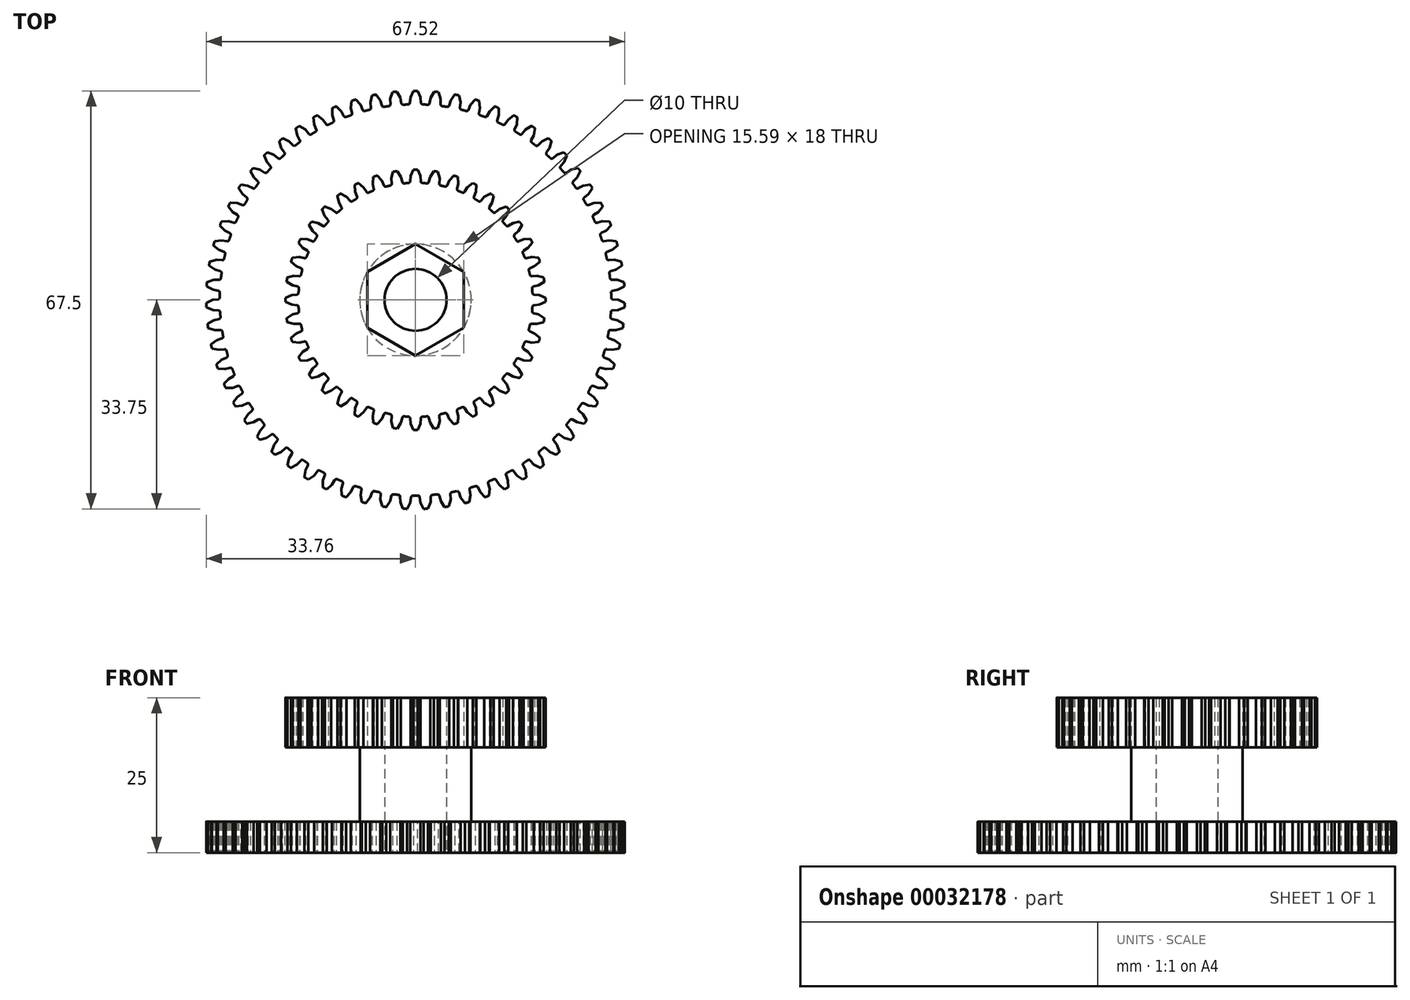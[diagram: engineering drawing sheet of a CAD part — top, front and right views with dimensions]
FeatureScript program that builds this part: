
annotation { "Feature Type Name" : "Feature", "Feature Type Description" : "" }
export const myFeature = defineFeature(function(context is Context, id is Id, definition is map)
    precondition{}
    {
        {
            var Q0;
            Q0=qCreatedBy(makeId("Top.planeOp"),FACE);
            var sketch = newSketch(context, id + "F0", { "sketchPlane" : qUnion([Q0])});
            skArc(sketch, "E0", {"start": v(31.82, 1.48) * mm, "mid": v(31.63, 1.37) * mm, "end": v(31.56, 1.16) * mm});
            skLineSegment(sketch, "E1", {"start": v(31.82, 1.48) * mm, "end": v(32.69, 1.63) * mm});
            skLineSegment(sketch, "E2", {"start": v(32.69, 1.63) * mm, "end": v(33.7, 2.16) * mm});
            skArc(sketch, "E3", {"start": v(31.39, 3.53) * mm, "mid": v(31.34, 3.91) * mm, "end": v(31.29, 4.3) * mm});
            skArc(sketch, "E4", {"start": v(31.81, -1.7) * mm, "mid": v(31.61, -1.79) * mm, "end": v(31.52, -1.99) * mm});
            skArc(sketch, "E5", {"start": v(31.52, 4.64) * mm, "mid": v(31.34, 4.51) * mm, "end": v(31.29, 4.3) * mm});
            skLineSegment(sketch, "E6", {"start": v(31.81, -1.7) * mm, "end": v(32.69, -1.63) * mm});
            skLineSegment(sketch, "E7", {"start": v(31.52, 4.64) * mm, "end": v(32.36, 4.88) * mm});
            skLineSegment(sketch, "E8", {"start": v(32.69, -1.63) * mm, "end": v(33.75, -1.2) * mm});
            skLineSegment(sketch, "E9", {"start": v(32.36, 4.88) * mm, "end": v(33.31, 5.5) * mm});
            skArc(sketch, "E10", {"start": v(30.88, 6.64) * mm, "mid": v(30.8, 7.02) * mm, "end": v(30.7, 7.4) * mm});
            skArc(sketch, "E11", {"start": v(31.49, -4.85) * mm, "mid": v(31.28, -4.93) * mm, "end": v(31.17, -5.12) * mm});
            skArc(sketch, "E12", {"start": v(30.9, 7.76) * mm, "mid": v(30.73, 7.61) * mm, "end": v(30.7, 7.4) * mm});
            skLineSegment(sketch, "E13", {"start": v(31.49, -4.85) * mm, "end": v(32.36, -4.88) * mm});
            skLineSegment(sketch, "E14", {"start": v(30.9, 7.76) * mm, "end": v(31.71, 8.07) * mm});
            skLineSegment(sketch, "E15", {"start": v(32.36, -4.88) * mm, "end": v(33.46, -4.56) * mm});
            skLineSegment(sketch, "E16", {"start": v(31.71, 8.07) * mm, "end": v(32.6, 8.8) * mm});
            skArc(sketch, "E17", {"start": v(30.06, 9.68) * mm, "mid": v(29.94, 10.05) * mm, "end": v(29.81, 10.41) * mm});
            skArc(sketch, "E18", {"start": v(30.85, -7.97) * mm, "mid": v(30.64, -8.02) * mm, "end": v(30.5, -8.2) * mm});
            skArc(sketch, "E19", {"start": v(29.97, 10.8) * mm, "mid": v(29.82, 10.63) * mm, "end": v(29.81, 10.41) * mm});
            skLineSegment(sketch, "E20", {"start": v(30.85, -7.97) * mm, "end": v(31.72, -8.08) * mm});
            skLineSegment(sketch, "E21", {"start": v(29.97, 10.8) * mm, "end": v(30.75, 11.2) * mm});
            skLineSegment(sketch, "E22", {"start": v(31.72, -8.08) * mm, "end": v(32.84, -7.86) * mm});
            skLineSegment(sketch, "E23", {"start": v(30.75, 11.2) * mm, "end": v(31.56, 12) * mm});
            skArc(sketch, "E24", {"start": v(28.95, 12.62) * mm, "mid": v(28.8, 12.98) * mm, "end": v(28.63, 13.33) * mm});
            skArc(sketch, "E25", {"start": v(29.9, -11) * mm, "mid": v(29.69, -11.03) * mm, "end": v(29.54, -11.2) * mm});
            skArc(sketch, "E26", {"start": v(28.74, 13.72) * mm, "mid": v(28.61, 13.55) * mm, "end": v(28.63, 13.33) * mm});
            skLineSegment(sketch, "E27", {"start": v(29.9, -11) * mm, "end": v(30.76, -11.2) * mm});
            skLineSegment(sketch, "E28", {"start": v(28.74, 13.72) * mm, "end": v(29.48, 14.2) * mm});
            skLineSegment(sketch, "E29", {"start": v(30.76, -11.2) * mm, "end": v(31.9, -11.1) * mm});
            skLineSegment(sketch, "E30", {"start": v(29.48, 14.2) * mm, "end": v(30.2, 15.08) * mm});
            skArc(sketch, "E31", {"start": v(27.55, 15.44) * mm, "mid": v(27.35, 15.78) * mm, "end": v(27.16, 16.11) * mm});
            skArc(sketch, "E32", {"start": v(28.66, -13.92) * mm, "mid": v(28.44, -13.93) * mm, "end": v(28.28, -14.08) * mm});
            skArc(sketch, "E33", {"start": v(27.23, 16.52) * mm, "mid": v(27.12, 16.33) * mm, "end": v(27.16, 16.11) * mm});
            skLineSegment(sketch, "E34", {"start": v(28.66, -13.92) * mm, "end": v(29.5, -14.2) * mm});
            skLineSegment(sketch, "E35", {"start": v(27.23, 16.52) * mm, "end": v(27.92, 17.06) * mm});
            skLineSegment(sketch, "E36", {"start": v(29.5, -14.2) * mm, "end": v(30.64, -14.22) * mm});
            skLineSegment(sketch, "E37", {"start": v(27.92, 17.06) * mm, "end": v(28.55, 18.02) * mm});
            skArc(sketch, "E38", {"start": v(25.87, 18.1) * mm, "mid": v(25.65, 18.42) * mm, "end": v(25.42, 18.74) * mm});
            skArc(sketch, "E39", {"start": v(27.13, -16.7) * mm, "mid": v(26.92, -16.69) * mm, "end": v(26.74, -16.82) * mm});
            skArc(sketch, "E40", {"start": v(25.45, 19.15) * mm, "mid": v(25.36, 18.95) * mm, "end": v(25.42, 18.74) * mm});
            skLineSegment(sketch, "E41", {"start": v(27.13, -16.7) * mm, "end": v(27.93, -17.07) * mm});
            skLineSegment(sketch, "E42", {"start": v(25.45, 19.15) * mm, "end": v(26.08, 19.76) * mm});
            skLineSegment(sketch, "E43", {"start": v(27.93, -17.07) * mm, "end": v(29.07, -17.2) * mm});
            skLineSegment(sketch, "E44", {"start": v(26.08, 19.76) * mm, "end": v(26.62, 20.77) * mm});
            skArc(sketch, "E45", {"start": v(23.94, 20.6) * mm, "mid": v(23.68, 20.89) * mm, "end": v(23.42, 21.18) * mm});
            skArc(sketch, "E46", {"start": v(25.34, -19.32) * mm, "mid": v(25.12, -19.29) * mm, "end": v(24.93, -19.4) * mm});
            skArc(sketch, "E47", {"start": v(23.42, 21.59) * mm, "mid": v(23.34, 21.38) * mm, "end": v(23.42, 21.18) * mm});
            skLineSegment(sketch, "E48", {"start": v(25.34, -19.32) * mm, "end": v(26.1, -19.77) * mm});
            skLineSegment(sketch, "E49", {"start": v(23.42, 21.59) * mm, "end": v(23.98, 22.26) * mm});
            skLineSegment(sketch, "E50", {"start": v(26.1, -19.77) * mm, "end": v(27.21, -20) * mm});
            skLineSegment(sketch, "E51", {"start": v(23.98, 22.26) * mm, "end": v(24.41, 23.32) * mm});
            skArc(sketch, "E52", {"start": v(21.77, 22.88) * mm, "mid": v(21.48, 23.14) * mm, "end": v(21.2, 23.4) * mm});
            skArc(sketch, "E53", {"start": v(23.29, -21.75) * mm, "mid": v(23.08, -21.7) * mm, "end": v(22.88, -21.79) * mm});
            skArc(sketch, "E54", {"start": v(21.15, 23.81) * mm, "mid": v(21.1, 23.6) * mm, "end": v(21.2, 23.4) * mm});
            skLineSegment(sketch, "E55", {"start": v(23.29, -21.75) * mm, "end": v(24, -22.27) * mm});
            skLineSegment(sketch, "E56", {"start": v(21.15, 23.81) * mm, "end": v(21.65, 24.53) * mm});
            skLineSegment(sketch, "E57", {"start": v(24, -22.27) * mm, "end": v(25.09, -22.62) * mm});
            skLineSegment(sketch, "E58", {"start": v(21.65, 24.53) * mm, "end": v(21.97, 25.63) * mm});
            skArc(sketch, "E59", {"start": v(19.38, 24.93) * mm, "mid": v(19.07, 25.16) * mm, "end": v(18.76, 25.4) * mm});
            skArc(sketch, "E60", {"start": v(21, -23.96) * mm, "mid": v(20.8, -23.88) * mm, "end": v(20.6, -23.96) * mm});
            skArc(sketch, "E61", {"start": v(18.67, 25.8) * mm, "mid": v(18.64, 25.58) * mm, "end": v(18.76, 25.4) * mm});
            skLineSegment(sketch, "E62", {"start": v(21, -23.96) * mm, "end": v(21.66, -24.55) * mm});
            skLineSegment(sketch, "E63", {"start": v(18.67, 25.8) * mm, "end": v(19.1, 26.57) * mm});
            skLineSegment(sketch, "E64", {"start": v(21.66, -24.55) * mm, "end": v(22.71, -25) * mm});
            skLineSegment(sketch, "E65", {"start": v(19.1, 26.57) * mm, "end": v(19.3, 27.7) * mm});
            skArc(sketch, "E66", {"start": v(16.8, 26.73) * mm, "mid": v(16.47, 26.94) * mm, "end": v(16.14, 27.14) * mm});
            skArc(sketch, "E67", {"start": v(18.52, -25.93) * mm, "mid": v(18.32, -25.84) * mm, "end": v(18.11, -25.89) * mm});
            skArc(sketch, "E68", {"start": v(16.01, 27.53) * mm, "mid": v(16, 27.3) * mm, "end": v(16.14, 27.14) * mm});
            skLineSegment(sketch, "E69", {"start": v(18.52, -25.93) * mm, "end": v(19.11, -26.58) * mm});
            skLineSegment(sketch, "E70", {"start": v(16.01, 27.53) * mm, "end": v(16.35, 28.34) * mm});
            skLineSegment(sketch, "E71", {"start": v(19.11, -26.58) * mm, "end": v(20.11, -27.14) * mm});
            skLineSegment(sketch, "E72", {"start": v(16.35, 28.34) * mm, "end": v(16.45, 29.47) * mm});
            skArc(sketch, "E73", {"start": v(14.05, 28.27) * mm, "mid": v(13.7, 28.44) * mm, "end": v(13.35, 28.61) * mm});
            skArc(sketch, "E74", {"start": v(15.85, -27.65) * mm, "mid": v(15.66, -27.53) * mm, "end": v(15.45, -27.56) * mm});
            skArc(sketch, "E75", {"start": v(13.19, 28.99) * mm, "mid": v(13.2, 28.77) * mm, "end": v(13.35, 28.61) * mm});
            skLineSegment(sketch, "E76", {"start": v(15.85, -27.65) * mm, "end": v(16.37, -28.35) * mm});
            skLineSegment(sketch, "E77", {"start": v(13.19, 28.99) * mm, "end": v(13.45, 29.82) * mm});
            skLineSegment(sketch, "E78", {"start": v(16.37, -28.35) * mm, "end": v(17.31, -29) * mm});
            skLineSegment(sketch, "E79", {"start": v(13.45, 29.82) * mm, "end": v(13.44, 30.97) * mm});
            skArc(sketch, "E80", {"start": v(11.17, 29.53) * mm, "mid": v(10.8, 29.67) * mm, "end": v(10.44, 29.8) * mm});
            skArc(sketch, "E81", {"start": v(13.02, -29.1) * mm, "mid": v(12.84, -28.95) * mm, "end": v(12.63, -28.97) * mm});
            skArc(sketch, "E82", {"start": v(10.24, 30.16) * mm, "mid": v(10.27, 29.94) * mm, "end": v(10.44, 29.8) * mm});
            skLineSegment(sketch, "E83", {"start": v(13.02, -29.1) * mm, "end": v(13.47, -29.84) * mm});
            skLineSegment(sketch, "E84", {"start": v(10.24, 30.16) * mm, "end": v(10.41, 31.01) * mm});
            skLineSegment(sketch, "E85", {"start": v(13.47, -29.84) * mm, "end": v(14.34, -30.59) * mm});
            skLineSegment(sketch, "E86", {"start": v(10.41, 31.01) * mm, "end": v(10.28, 32.15) * mm});
            skArc(sketch, "E87", {"start": v(8.17, 30.5) * mm, "mid": v(7.8, 30.6) * mm, "end": v(7.42, 30.69) * mm});
            skArc(sketch, "E88", {"start": v(10.06, -30.24) * mm, "mid": v(9.9, -30.09) * mm, "end": v(9.68, -30.08) * mm});
            skArc(sketch, "E89", {"start": v(7.18, 31.02) * mm, "mid": v(7.24, 30.81) * mm, "end": v(7.42, 30.69) * mm});
            skLineSegment(sketch, "E90", {"start": v(10.06, -30.24) * mm, "end": v(10.43, -31.03) * mm});
            skLineSegment(sketch, "E91", {"start": v(7.18, 31.02) * mm, "end": v(7.27, 31.9) * mm});
            skLineSegment(sketch, "E92", {"start": v(10.43, -31.03) * mm, "end": v(11.22, -31.86) * mm});
            skLineSegment(sketch, "E93", {"start": v(7.27, 31.9) * mm, "end": v(7.03, 33.01) * mm});
            skArc(sketch, "E94", {"start": v(5.1, 31.16) * mm, "mid": v(4.7, 31.22) * mm, "end": v(4.32, 31.27) * mm});
            skArc(sketch, "E95", {"start": v(7, -31.1) * mm, "mid": v(6.86, -30.93) * mm, "end": v(6.64, -30.9) * mm});
            skArc(sketch, "E96", {"start": v(4.05, 31.59) * mm, "mid": v(4.13, 31.38) * mm, "end": v(4.32, 31.27) * mm});
            skLineSegment(sketch, "E97", {"start": v(7, -31.1) * mm, "end": v(7.3, -31.92) * mm});
            skLineSegment(sketch, "E98", {"start": v(4.05, 31.59) * mm, "end": v(4.06, 32.46) * mm});
            skLineSegment(sketch, "E99", {"start": v(7.3, -31.92) * mm, "end": v(8, -32.82) * mm});
            skLineSegment(sketch, "E100", {"start": v(4.06, 32.46) * mm, "end": v(3.7, 33.55) * mm});
            skArc(sketch, "E101", {"start": v(1.96, 31.51) * mm, "mid": v(1.57, 31.53) * mm, "end": v(1.19, 31.55) * mm});
            skArc(sketch, "E102", {"start": v(3.87, -31.64) * mm, "mid": v(3.74, -31.45) * mm, "end": v(3.53, -31.4) * mm});
            skArc(sketch, "E103", {"start": v(0.89, 31.83) * mm, "mid": v(0.98, 31.63) * mm, "end": v(1.19, 31.55) * mm});
            skLineSegment(sketch, "E104", {"start": v(3.87, -31.64) * mm, "end": v(4.08, -32.49) * mm});
            skLineSegment(sketch, "E105", {"start": v(0.89, 31.83) * mm, "end": v(0.8, 32.7) * mm});
            skLineSegment(sketch, "E106", {"start": v(4.08, -32.49) * mm, "end": v(4.69, -33.45) * mm});
            skLineSegment(sketch, "E107", {"start": v(0.8, 32.7) * mm, "end": v(0.35, 33.75) * mm});
            skArc(sketch, "E108", {"start": v(-1.19, 31.55) * mm, "mid": v(-1.57, 31.53) * mm, "end": v(-1.96, 31.51) * mm});
            skArc(sketch, "E109", {"start": v(0.7, -31.86) * mm, "mid": v(0.6, -31.67) * mm, "end": v(0.39, -31.6) * mm});
            skArc(sketch, "E110", {"start": v(-2.29, 31.76) * mm, "mid": v(-2.17, 31.58) * mm, "end": v(-1.96, 31.51) * mm});
            skLineSegment(sketch, "E111", {"start": v(0.7, -31.86) * mm, "end": v(0.83, -32.73) * mm});
            skLineSegment(sketch, "E112", {"start": v(-2.29, 31.76) * mm, "end": v(-2.46, 32.62) * mm});
            skLineSegment(sketch, "E113", {"start": v(0.83, -32.73) * mm, "end": v(1.34, -33.75) * mm});
            skLineSegment(sketch, "E114", {"start": v(-2.46, 32.62) * mm, "end": v(-3.02, 33.62) * mm});
            skArc(sketch, "E115", {"start": v(-4.32, 31.27) * mm, "mid": v(-4.7, 31.22) * mm, "end": v(-5.1, 31.16) * mm});
            skArc(sketch, "E116", {"start": v(-2.47, -31.77) * mm, "mid": v(-2.56, -31.57) * mm, "end": v(-2.76, -31.48) * mm});
            skArc(sketch, "E117", {"start": v(-5.44, 31.38) * mm, "mid": v(-5.3, 31.2) * mm, "end": v(-5.1, 31.16) * mm});
            skLineSegment(sketch, "E118", {"start": v(-2.47, -31.77) * mm, "end": v(-2.44, -32.65) * mm});
            skLineSegment(sketch, "E119", {"start": v(-5.44, 31.38) * mm, "end": v(-5.7, 32.22) * mm});
            skLineSegment(sketch, "E120", {"start": v(-2.44, -32.65) * mm, "end": v(-2.03, -33.72) * mm});
            skLineSegment(sketch, "E121", {"start": v(-5.7, 32.22) * mm, "end": v(-6.35, 33.15) * mm});
            skArc(sketch, "E122", {"start": v(-7.42, 30.69) * mm, "mid": v(-7.8, 30.6) * mm, "end": v(-8.17, 30.5) * mm});
            skArc(sketch, "E123", {"start": v(-5.62, -31.37) * mm, "mid": v(-5.7, -31.16) * mm, "end": v(-5.88, -31.05) * mm});
            skArc(sketch, "E124", {"start": v(-8.54, 30.68) * mm, "mid": v(-8.39, 30.52) * mm, "end": v(-8.17, 30.5) * mm});
            skLineSegment(sketch, "E125", {"start": v(-5.62, -31.37) * mm, "end": v(-5.67, -32.25) * mm});
            skLineSegment(sketch, "E126", {"start": v(-8.54, 30.68) * mm, "end": v(-8.87, 31.49) * mm});
            skLineSegment(sketch, "E127", {"start": v(-5.67, -32.25) * mm, "end": v(-5.38, -33.35) * mm});
            skLineSegment(sketch, "E128", {"start": v(-8.87, 31.49) * mm, "end": v(-9.62, 32.35) * mm});
            skArc(sketch, "E129", {"start": v(-10.44, 29.8) * mm, "mid": v(-10.8, 29.67) * mm, "end": v(-11.17, 29.53) * mm});
            skArc(sketch, "E130", {"start": v(-8.72, -30.65) * mm, "mid": v(-8.76, -30.44) * mm, "end": v(-8.94, -30.3) * mm});
            skArc(sketch, "E131", {"start": v(-11.55, 29.68) * mm, "mid": v(-11.39, 29.53) * mm, "end": v(-11.17, 29.53) * mm});
            skLineSegment(sketch, "E132", {"start": v(-8.72, -30.65) * mm, "end": v(-8.85, -31.52) * mm});
            skLineSegment(sketch, "E133", {"start": v(-11.55, 29.68) * mm, "end": v(-11.97, 30.45) * mm});
            skLineSegment(sketch, "E134", {"start": v(-8.85, -31.52) * mm, "end": v(-8.67, -32.65) * mm});
            skLineSegment(sketch, "E135", {"start": v(-11.97, 30.45) * mm, "end": v(-12.8, 31.24) * mm});
            skArc(sketch, "E136", {"start": v(-13.35, 28.61) * mm, "mid": v(-13.7, 28.44) * mm, "end": v(-14.05, 28.27) * mm});
            skArc(sketch, "E137", {"start": v(-11.73, -29.63) * mm, "mid": v(-11.75, -29.42) * mm, "end": v(-11.91, -29.27) * mm});
            skArc(sketch, "E138", {"start": v(-14.45, 28.38) * mm, "mid": v(-14.27, 28.25) * mm, "end": v(-14.05, 28.27) * mm});
            skLineSegment(sketch, "E139", {"start": v(-11.73, -29.63) * mm, "end": v(-11.95, -30.48) * mm});
            skLineSegment(sketch, "E140", {"start": v(-14.45, 28.38) * mm, "end": v(-14.94, 29.1) * mm});
            skLineSegment(sketch, "E141", {"start": v(-11.95, -30.48) * mm, "end": v(-11.87, -31.62) * mm});
            skLineSegment(sketch, "E142", {"start": v(-14.94, 29.1) * mm, "end": v(-15.84, 29.8) * mm});
            skArc(sketch, "E143", {"start": v(-16.14, 27.14) * mm, "mid": v(-16.47, 26.94) * mm, "end": v(-16.8, 26.73) * mm});
            skArc(sketch, "E144", {"start": v(-14.62, -28.32) * mm, "mid": v(-14.62, -28.1) * mm, "end": v(-14.76, -27.94) * mm});
            skArc(sketch, "E145", {"start": v(-17.2, 26.8) * mm, "mid": v(-17.01, 26.7) * mm, "end": v(-16.8, 26.73) * mm});
            skLineSegment(sketch, "E146", {"start": v(-14.62, -28.32) * mm, "end": v(-14.92, -29.14) * mm});
            skLineSegment(sketch, "E147", {"start": v(-17.2, 26.8) * mm, "end": v(-17.77, 27.47) * mm});
            skLineSegment(sketch, "E148", {"start": v(-14.92, -29.14) * mm, "end": v(-14.96, -30.28) * mm});
            skLineSegment(sketch, "E149", {"start": v(-17.77, 27.47) * mm, "end": v(-18.73, 28.08) * mm});
            skArc(sketch, "E150", {"start": v(-18.76, 25.4) * mm, "mid": v(-19.07, 25.16) * mm, "end": v(-19.38, 24.93) * mm});
            skArc(sketch, "E151", {"start": v(-17.36, -26.72) * mm, "mid": v(-17.34, -26.5) * mm, "end": v(-17.47, -26.33) * mm});
            skArc(sketch, "E152", {"start": v(-19.79, 24.95) * mm, "mid": v(-19.59, 24.86) * mm, "end": v(-19.38, 24.93) * mm});
            skLineSegment(sketch, "E153", {"start": v(-17.36, -26.72) * mm, "end": v(-17.75, -27.51) * mm});
            skLineSegment(sketch, "E154", {"start": v(-19.79, 24.95) * mm, "end": v(-20.41, 25.57) * mm});
            skLineSegment(sketch, "E155", {"start": v(-17.75, -27.51) * mm, "end": v(-17.9, -28.64) * mm});
            skLineSegment(sketch, "E156", {"start": v(-20.41, 25.57) * mm, "end": v(-21.44, 26.08) * mm});
            skArc(sketch, "E157", {"start": v(-21.2, 23.4) * mm, "mid": v(-21.48, 23.14) * mm, "end": v(-21.77, 22.88) * mm});
            skArc(sketch, "E158", {"start": v(-19.94, -24.86) * mm, "mid": v(-19.9, -24.65) * mm, "end": v(-20, -24.46) * mm});
            skArc(sketch, "E159", {"start": v(-22.18, 22.86) * mm, "mid": v(-21.97, 22.79) * mm, "end": v(-21.77, 22.88) * mm});
            skLineSegment(sketch, "E160", {"start": v(-19.94, -24.86) * mm, "end": v(-20.4, -25.6) * mm});
            skLineSegment(sketch, "E161", {"start": v(-22.18, 22.86) * mm, "end": v(-22.86, 23.4) * mm});
            skLineSegment(sketch, "E162", {"start": v(-20.4, -25.6) * mm, "end": v(-20.66, -26.72) * mm});
            skLineSegment(sketch, "E163", {"start": v(-22.86, 23.4) * mm, "end": v(-23.93, 23.81) * mm});
            skArc(sketch, "E164", {"start": v(-23.42, 21.18) * mm, "mid": v(-23.68, 20.89) * mm, "end": v(-23.94, 20.6) * mm});
            skArc(sketch, "E165", {"start": v(-22.31, -22.75) * mm, "mid": v(-22.25, -22.54) * mm, "end": v(-22.34, -22.34) * mm});
            skArc(sketch, "E166", {"start": v(-24.34, 20.54) * mm, "mid": v(-24.13, 20.49) * mm, "end": v(-23.94, 20.6) * mm});
            skLineSegment(sketch, "E167", {"start": v(-22.31, -22.75) * mm, "end": v(-22.84, -23.45) * mm});
            skLineSegment(sketch, "E168", {"start": v(-24.34, 20.54) * mm, "end": v(-25.08, 21.02) * mm});
            skLineSegment(sketch, "E169", {"start": v(-22.84, -23.45) * mm, "end": v(-23.22, -24.53) * mm});
            skLineSegment(sketch, "E170", {"start": v(-25.08, 21.02) * mm, "end": v(-26.18, 21.31) * mm});
            skArc(sketch, "E171", {"start": v(-25.42, 18.74) * mm, "mid": v(-25.65, 18.42) * mm, "end": v(-25.87, 18.1) * mm});
            skArc(sketch, "E172", {"start": v(-24.46, -20.42) * mm, "mid": v(-24.38, -20.22) * mm, "end": v(-24.45, -20) * mm});
            skArc(sketch, "E173", {"start": v(-26.27, 18.01) * mm, "mid": v(-26.05, 17.98) * mm, "end": v(-25.87, 18.1) * mm});
            skLineSegment(sketch, "E174", {"start": v(-24.46, -20.42) * mm, "end": v(-25.06, -21.06) * mm});
            skLineSegment(sketch, "E175", {"start": v(-26.27, 18.01) * mm, "end": v(-27.05, 18.41) * mm});
            skLineSegment(sketch, "E176", {"start": v(-25.06, -21.06) * mm, "end": v(-25.55, -22.1) * mm});
            skLineSegment(sketch, "E177", {"start": v(-27.05, 18.41) * mm, "end": v(-28.18, 18.6) * mm});
            skArc(sketch, "E178", {"start": v(-27.16, 16.11) * mm, "mid": v(-27.35, 15.78) * mm, "end": v(-27.55, 15.44) * mm});
            skArc(sketch, "E179", {"start": v(-26.37, -17.88) * mm, "mid": v(-26.27, -17.69) * mm, "end": v(-26.32, -17.47) * mm});
            skArc(sketch, "E180", {"start": v(-27.93, 15.3) * mm, "mid": v(-27.71, 15.3) * mm, "end": v(-27.55, 15.44) * mm});
            skLineSegment(sketch, "E181", {"start": v(-26.37, -17.88) * mm, "end": v(-27.04, -18.46) * mm});
            skLineSegment(sketch, "E182", {"start": v(-27.93, 15.3) * mm, "end": v(-28.75, 15.63) * mm});
            skLineSegment(sketch, "E183", {"start": v(-27.04, -18.46) * mm, "end": v(-27.62, -19.44) * mm});
            skLineSegment(sketch, "E184", {"start": v(-28.75, 15.63) * mm, "end": v(-29.89, 15.7) * mm});
            skArc(sketch, "E185", {"start": v(-28.63, 13.33) * mm, "mid": v(-28.8, 12.98) * mm, "end": v(-28.95, 12.62) * mm});
            skArc(sketch, "E186", {"start": v(-28.02, -15.17) * mm, "mid": v(-27.9, -14.98) * mm, "end": v(-27.93, -14.77) * mm});
            skArc(sketch, "E187", {"start": v(-29.32, 12.45) * mm, "mid": v(-29.1, 12.47) * mm, "end": v(-28.95, 12.62) * mm});
            skLineSegment(sketch, "E188", {"start": v(-28.02, -15.17) * mm, "end": v(-28.74, -15.68) * mm});
            skLineSegment(sketch, "E189", {"start": v(-29.32, 12.45) * mm, "end": v(-30.16, 12.69) * mm});
            skLineSegment(sketch, "E190", {"start": v(-28.74, -15.68) * mm, "end": v(-29.42, -16.6) * mm});
            skLineSegment(sketch, "E191", {"start": v(-30.16, 12.69) * mm, "end": v(-31.3, 12.65) * mm});
            skArc(sketch, "E192", {"start": v(-29.82, 10.41) * mm, "mid": v(-29.94, 10.05) * mm, "end": v(-30.06, 9.68) * mm});
            skArc(sketch, "E193", {"start": v(-29.4, -12.3) * mm, "mid": v(-29.25, -12.13) * mm, "end": v(-29.26, -11.91) * mm});
            skArc(sketch, "E194", {"start": v(-30.41, 9.47) * mm, "mid": v(-30.2, 9.5) * mm, "end": v(-30.06, 9.68) * mm});
            skLineSegment(sketch, "E195", {"start": v(-29.4, -12.3) * mm, "end": v(-30.15, -12.74) * mm});
            skLineSegment(sketch, "E196", {"start": v(-30.41, 9.47) * mm, "end": v(-31.28, 9.62) * mm});
            skLineSegment(sketch, "E197", {"start": v(-30.15, -12.74) * mm, "end": v(-30.92, -13.58) * mm});
            skLineSegment(sketch, "E198", {"start": v(-31.28, 9.62) * mm, "end": v(-32.4, 9.47) * mm});
            skArc(sketch, "E199", {"start": v(-30.7, 7.4) * mm, "mid": v(-30.8, 7.02) * mm, "end": v(-30.88, 6.64) * mm});
            skArc(sketch, "E200", {"start": v(-30.47, -9.31) * mm, "mid": v(-30.31, -9.16) * mm, "end": v(-30.3, -8.94) * mm});
            skArc(sketch, "E201", {"start": v(-31.2, 6.4) * mm, "mid": v(-31, 6.45) * mm, "end": v(-30.88, 6.64) * mm});
            skLineSegment(sketch, "E202", {"start": v(-30.47, -9.31) * mm, "end": v(-31.27, -9.67) * mm});
            skLineSegment(sketch, "E203", {"start": v(-31.2, 6.4) * mm, "end": v(-32.08, 6.46) * mm});
            skLineSegment(sketch, "E204", {"start": v(-31.27, -9.67) * mm, "end": v(-32.12, -10.44) * mm});
            skLineSegment(sketch, "E205", {"start": v(-32.08, 6.46) * mm, "end": v(-33.2, 6.2) * mm});
            skArc(sketch, "E206", {"start": v(-31.29, 4.3) * mm, "mid": v(-31.34, 3.91) * mm, "end": v(-31.39, 3.53) * mm});
            skArc(sketch, "E207", {"start": v(-31.24, -6.23) * mm, "mid": v(-31.07, -6.1) * mm, "end": v(-31.04, -5.88) * mm});
            skArc(sketch, "E208", {"start": v(-31.69, 3.25) * mm, "mid": v(-31.49, 3.33) * mm, "end": v(-31.39, 3.53) * mm});
            skLineSegment(sketch, "E209", {"start": v(-31.24, -6.23) * mm, "end": v(-32.08, -6.5) * mm});
            skLineSegment(sketch, "E210", {"start": v(-31.69, 3.25) * mm, "end": v(-32.57, 3.23) * mm});
            skLineSegment(sketch, "E211", {"start": v(-32.08, -6.5) * mm, "end": v(-33, -7.19) * mm});
            skLineSegment(sketch, "E212", {"start": v(-32.57, 3.23) * mm, "end": v(-33.65, 2.86) * mm});
            skArc(sketch, "E213", {"start": v(-31.7, -3.1) * mm, "mid": v(-31.52, -2.97) * mm, "end": v(-31.47, -2.76) * mm});
            skArc(sketch, "E214", {"start": v(-31.56, 1.16) * mm, "mid": v(-31.58, 0.77) * mm, "end": v(-31.58, 0.39) * mm});
            skLineSegment(sketch, "E215", {"start": v(-31.7, -3.1) * mm, "end": v(-32.56, -3.28) * mm});
            skArc(sketch, "E216", {"start": v(-31.86, 0.08) * mm, "mid": v(-31.66, 0.18) * mm, "end": v(-31.58, 0.39) * mm});
            skLineSegment(sketch, "E217", {"start": v(-32.56, -3.28) * mm, "end": v(-33.55, -3.87) * mm});
            skLineSegment(sketch, "E218", {"start": v(-31.86, 0.08) * mm, "end": v(-32.73, -0.02) * mm});
            skLineSegment(sketch, "E219", {"start": v(-32.73, -0.02) * mm, "end": v(-33.76, -0.5) * mm});
            skLineSegment(sketch, "E220", {"start": v(-33.75, -1.2) * mm, "end": v(-32.69, -1.63) * mm});
            skLineSegment(sketch, "E221", {"start": v(-32.69, -1.63) * mm, "end": v(-31.81, -1.7) * mm});
            skArc(sketch, "E222", {"start": v(-31.52, -1.99) * mm, "mid": v(-31.61, -1.79) * mm, "end": v(-31.81, -1.7) * mm});
            skArc(sketch, "E223", {"start": v(-31.52, -1.99) * mm, "mid": v(-31.5, -2.37) * mm, "end": v(-31.47, -2.76) * mm});
            skLineSegment(sketch, "E224", {"start": v(-33.46, -4.56) * mm, "end": v(-32.36, -4.88) * mm});
            skLineSegment(sketch, "E225", {"start": v(-32.36, -4.88) * mm, "end": v(-31.49, -4.85) * mm});
            skArc(sketch, "E226", {"start": v(-31.17, -5.12) * mm, "mid": v(-31.28, -4.93) * mm, "end": v(-31.49, -4.85) * mm});
            skArc(sketch, "E227", {"start": v(-31.17, -5.12) * mm, "mid": v(-31.1, -5.5) * mm, "end": v(-31.04, -5.88) * mm});
            skLineSegment(sketch, "E228", {"start": v(-32.84, -7.86) * mm, "end": v(-31.72, -8.08) * mm});
            skLineSegment(sketch, "E229", {"start": v(-31.72, -8.08) * mm, "end": v(-30.85, -7.97) * mm});
            skArc(sketch, "E230", {"start": v(-30.5, -8.2) * mm, "mid": v(-30.64, -8.02) * mm, "end": v(-30.85, -7.97) * mm});
            skArc(sketch, "E231", {"start": v(-30.5, -8.2) * mm, "mid": v(-30.4, -8.57) * mm, "end": v(-30.3, -8.94) * mm});
            skLineSegment(sketch, "E232", {"start": v(-31.9, -11.1) * mm, "end": v(-30.76, -11.2) * mm});
            skLineSegment(sketch, "E233", {"start": v(-30.76, -11.2) * mm, "end": v(-29.9, -11) * mm});
            skArc(sketch, "E234", {"start": v(-29.54, -11.2) * mm, "mid": v(-29.69, -11.03) * mm, "end": v(-29.9, -11) * mm});
            skArc(sketch, "E235", {"start": v(-29.54, -11.2) * mm, "mid": v(-29.4, -11.55) * mm, "end": v(-29.26, -11.91) * mm});
            skLineSegment(sketch, "E236", {"start": v(-30.64, -14.22) * mm, "end": v(-29.5, -14.2) * mm});
            skLineSegment(sketch, "E237", {"start": v(-29.5, -14.2) * mm, "end": v(-28.66, -13.92) * mm});
            skArc(sketch, "E238", {"start": v(-28.28, -14.08) * mm, "mid": v(-28.44, -13.93) * mm, "end": v(-28.66, -13.92) * mm});
            skArc(sketch, "E239", {"start": v(-28.28, -14.08) * mm, "mid": v(-28.1, -14.42) * mm, "end": v(-27.93, -14.77) * mm});
            skLineSegment(sketch, "E240", {"start": v(-29.07, -17.2) * mm, "end": v(-27.93, -17.07) * mm});
            skLineSegment(sketch, "E241", {"start": v(-27.93, -17.07) * mm, "end": v(-27.13, -16.7) * mm});
            skArc(sketch, "E242", {"start": v(-26.74, -16.82) * mm, "mid": v(-26.92, -16.69) * mm, "end": v(-27.13, -16.7) * mm});
            skArc(sketch, "E243", {"start": v(-26.74, -16.82) * mm, "mid": v(-26.53, -17.15) * mm, "end": v(-26.32, -17.47) * mm});
            skLineSegment(sketch, "E244", {"start": v(-27.21, -20) * mm, "end": v(-26.1, -19.77) * mm});
            skLineSegment(sketch, "E245", {"start": v(-26.1, -19.77) * mm, "end": v(-25.34, -19.32) * mm});
            skArc(sketch, "E246", {"start": v(-24.93, -19.4) * mm, "mid": v(-25.12, -19.29) * mm, "end": v(-25.34, -19.32) * mm});
            skArc(sketch, "E247", {"start": v(-24.93, -19.4) * mm, "mid": v(-24.7, -19.7) * mm, "end": v(-24.45, -20) * mm});
            skLineSegment(sketch, "E248", {"start": v(-25.09, -22.62) * mm, "end": v(-24, -22.27) * mm});
            skLineSegment(sketch, "E249", {"start": v(-24, -22.27) * mm, "end": v(-23.29, -21.75) * mm});
            skArc(sketch, "E250", {"start": v(-22.88, -21.79) * mm, "mid": v(-23.08, -21.7) * mm, "end": v(-23.29, -21.75) * mm});
            skArc(sketch, "E251", {"start": v(-22.88, -21.79) * mm, "mid": v(-22.61, -22.07) * mm, "end": v(-22.34, -22.34) * mm});
            skLineSegment(sketch, "E252", {"start": v(-22.71, -25) * mm, "end": v(-21.66, -24.55) * mm});
            skLineSegment(sketch, "E253", {"start": v(-21.66, -24.55) * mm, "end": v(-21, -23.96) * mm});
            skArc(sketch, "E254", {"start": v(-20.6, -23.96) * mm, "mid": v(-20.8, -23.88) * mm, "end": v(-21, -23.96) * mm});
            skArc(sketch, "E255", {"start": v(-20.6, -23.96) * mm, "mid": v(-20.3, -24.2) * mm, "end": v(-20, -24.46) * mm});
            skLineSegment(sketch, "E256", {"start": v(-20.11, -27.14) * mm, "end": v(-19.11, -26.58) * mm});
            skLineSegment(sketch, "E257", {"start": v(-19.11, -26.58) * mm, "end": v(-18.52, -25.93) * mm});
            skArc(sketch, "E258", {"start": v(-18.11, -25.89) * mm, "mid": v(-18.32, -25.84) * mm, "end": v(-18.52, -25.93) * mm});
            skArc(sketch, "E259", {"start": v(-18.11, -25.89) * mm, "mid": v(-17.8, -26.11) * mm, "end": v(-17.47, -26.33) * mm});
            skLineSegment(sketch, "E260", {"start": v(-17.31, -29) * mm, "end": v(-16.37, -28.35) * mm});
            skLineSegment(sketch, "E261", {"start": v(-16.37, -28.35) * mm, "end": v(-15.85, -27.65) * mm});
            skArc(sketch, "E262", {"start": v(-15.45, -27.56) * mm, "mid": v(-15.66, -27.53) * mm, "end": v(-15.85, -27.65) * mm});
            skArc(sketch, "E263", {"start": v(-15.45, -27.56) * mm, "mid": v(-15.1, -27.75) * mm, "end": v(-14.76, -27.94) * mm});
            skLineSegment(sketch, "E264", {"start": v(-14.34, -30.59) * mm, "end": v(-13.47, -29.84) * mm});
            skLineSegment(sketch, "E265", {"start": v(-13.47, -29.84) * mm, "end": v(-13.02, -29.1) * mm});
            skArc(sketch, "E266", {"start": v(-12.63, -28.97) * mm, "mid": v(-12.84, -28.95) * mm, "end": v(-13.02, -29.1) * mm});
            skArc(sketch, "E267", {"start": v(-12.63, -28.97) * mm, "mid": v(-12.27, -29.12) * mm, "end": v(-11.91, -29.27) * mm});
            skLineSegment(sketch, "E268", {"start": v(-11.22, -31.86) * mm, "end": v(-10.43, -31.03) * mm});
            skLineSegment(sketch, "E269", {"start": v(-10.43, -31.03) * mm, "end": v(-10.06, -30.24) * mm});
            skArc(sketch, "E270", {"start": v(-9.68, -30.08) * mm, "mid": v(-9.9, -30.09) * mm, "end": v(-10.06, -30.24) * mm});
            skArc(sketch, "E271", {"start": v(-9.68, -30.08) * mm, "mid": v(-9.3, -30.2) * mm, "end": v(-8.94, -30.3) * mm});
            skLineSegment(sketch, "E272", {"start": v(-8, -32.82) * mm, "end": v(-7.3, -31.92) * mm});
            skLineSegment(sketch, "E273", {"start": v(-7.3, -31.92) * mm, "end": v(-7, -31.1) * mm});
            skArc(sketch, "E274", {"start": v(-6.64, -30.9) * mm, "mid": v(-6.86, -30.93) * mm, "end": v(-7, -31.1) * mm});
            skArc(sketch, "E275", {"start": v(-6.64, -30.9) * mm, "mid": v(-6.26, -30.97) * mm, "end": v(-5.88, -31.05) * mm});
            skLineSegment(sketch, "E276", {"start": v(-4.69, -33.45) * mm, "end": v(-4.08, -32.49) * mm});
            skLineSegment(sketch, "E277", {"start": v(-4.08, -32.49) * mm, "end": v(-3.87, -31.64) * mm});
            skArc(sketch, "E278", {"start": v(-3.53, -31.4) * mm, "mid": v(-3.74, -31.45) * mm, "end": v(-3.87, -31.64) * mm});
            skArc(sketch, "E279", {"start": v(-3.53, -31.4) * mm, "mid": v(-3.14, -31.44) * mm, "end": v(-2.76, -31.48) * mm});
            skLineSegment(sketch, "E280", {"start": v(-1.34, -33.75) * mm, "end": v(-0.83, -32.73) * mm});
            skLineSegment(sketch, "E281", {"start": v(-0.83, -32.73) * mm, "end": v(-0.7, -31.86) * mm});
            skArc(sketch, "E282", {"start": v(-0.39, -31.6) * mm, "mid": v(-0.6, -31.67) * mm, "end": v(-0.7, -31.86) * mm});
            skArc(sketch, "E283", {"start": v(-0.39, -31.6) * mm, "mid": v(0, -31.6) * mm, "end": v(0.39, -31.6) * mm});
            skLineSegment(sketch, "E284", {"start": v(2.03, -33.72) * mm, "end": v(2.44, -32.65) * mm});
            skLineSegment(sketch, "E285", {"start": v(2.44, -32.65) * mm, "end": v(2.47, -31.77) * mm});
            skArc(sketch, "E286", {"start": v(2.76, -31.48) * mm, "mid": v(2.56, -31.57) * mm, "end": v(2.47, -31.77) * mm});
            skArc(sketch, "E287", {"start": v(2.76, -31.48) * mm, "mid": v(3.14, -31.44) * mm, "end": v(3.53, -31.4) * mm});
            skLineSegment(sketch, "E288", {"start": v(5.38, -33.35) * mm, "end": v(5.67, -32.25) * mm});
            skLineSegment(sketch, "E289", {"start": v(5.67, -32.25) * mm, "end": v(5.62, -31.37) * mm});
            skArc(sketch, "E290", {"start": v(5.88, -31.05) * mm, "mid": v(5.7, -31.16) * mm, "end": v(5.62, -31.37) * mm});
            skArc(sketch, "E291", {"start": v(5.88, -31.05) * mm, "mid": v(6.26, -30.97) * mm, "end": v(6.64, -30.9) * mm});
            skLineSegment(sketch, "E292", {"start": v(8.67, -32.65) * mm, "end": v(8.85, -31.52) * mm});
            skLineSegment(sketch, "E293", {"start": v(8.85, -31.52) * mm, "end": v(8.72, -30.65) * mm});
            skArc(sketch, "E294", {"start": v(8.94, -30.3) * mm, "mid": v(8.76, -30.44) * mm, "end": v(8.72, -30.65) * mm});
            skArc(sketch, "E295", {"start": v(8.94, -30.3) * mm, "mid": v(9.3, -30.2) * mm, "end": v(9.68, -30.08) * mm});
            skLineSegment(sketch, "E296", {"start": v(11.87, -31.62) * mm, "end": v(11.95, -30.48) * mm});
            skLineSegment(sketch, "E297", {"start": v(11.95, -30.48) * mm, "end": v(11.73, -29.63) * mm});
            skArc(sketch, "E298", {"start": v(11.91, -29.27) * mm, "mid": v(11.75, -29.42) * mm, "end": v(11.73, -29.63) * mm});
            skArc(sketch, "E299", {"start": v(11.91, -29.27) * mm, "mid": v(12.27, -29.12) * mm, "end": v(12.63, -28.97) * mm});
            skLineSegment(sketch, "E300", {"start": v(14.96, -30.28) * mm, "end": v(14.92, -29.14) * mm});
            skLineSegment(sketch, "E301", {"start": v(14.92, -29.14) * mm, "end": v(14.62, -28.32) * mm});
            skArc(sketch, "E302", {"start": v(14.76, -27.94) * mm, "mid": v(14.62, -28.1) * mm, "end": v(14.62, -28.32) * mm});
            skArc(sketch, "E303", {"start": v(14.76, -27.94) * mm, "mid": v(15.1, -27.75) * mm, "end": v(15.45, -27.56) * mm});
            skLineSegment(sketch, "E304", {"start": v(17.9, -28.64) * mm, "end": v(17.75, -27.51) * mm});
            skLineSegment(sketch, "E305", {"start": v(17.75, -27.51) * mm, "end": v(17.36, -26.72) * mm});
            skArc(sketch, "E306", {"start": v(17.47, -26.33) * mm, "mid": v(17.34, -26.5) * mm, "end": v(17.36, -26.72) * mm});
            skArc(sketch, "E307", {"start": v(17.47, -26.33) * mm, "mid": v(17.8, -26.11) * mm, "end": v(18.11, -25.89) * mm});
            skLineSegment(sketch, "E308", {"start": v(20.66, -26.72) * mm, "end": v(20.4, -25.6) * mm});
            skLineSegment(sketch, "E309", {"start": v(20.4, -25.6) * mm, "end": v(19.94, -24.86) * mm});
            skArc(sketch, "E310", {"start": v(20, -24.46) * mm, "mid": v(19.9, -24.65) * mm, "end": v(19.94, -24.86) * mm});
            skArc(sketch, "E311", {"start": v(20, -24.46) * mm, "mid": v(20.3, -24.2) * mm, "end": v(20.6, -23.96) * mm});
            skLineSegment(sketch, "E312", {"start": v(23.22, -24.53) * mm, "end": v(22.84, -23.45) * mm});
            skLineSegment(sketch, "E313", {"start": v(22.84, -23.45) * mm, "end": v(22.31, -22.75) * mm});
            skArc(sketch, "E314", {"start": v(22.34, -22.34) * mm, "mid": v(22.25, -22.54) * mm, "end": v(22.31, -22.75) * mm});
            skArc(sketch, "E315", {"start": v(22.34, -22.34) * mm, "mid": v(22.61, -22.07) * mm, "end": v(22.88, -21.79) * mm});
            skLineSegment(sketch, "E316", {"start": v(25.55, -22.1) * mm, "end": v(25.06, -21.06) * mm});
            skLineSegment(sketch, "E317", {"start": v(25.06, -21.06) * mm, "end": v(24.46, -20.42) * mm});
            skArc(sketch, "E318", {"start": v(24.45, -20) * mm, "mid": v(24.38, -20.22) * mm, "end": v(24.46, -20.42) * mm});
            skArc(sketch, "E319", {"start": v(24.45, -20) * mm, "mid": v(24.7, -19.7) * mm, "end": v(24.93, -19.4) * mm});
            skLineSegment(sketch, "E320", {"start": v(27.62, -19.44) * mm, "end": v(27.04, -18.46) * mm});
            skLineSegment(sketch, "E321", {"start": v(27.04, -18.46) * mm, "end": v(26.37, -17.88) * mm});
            skArc(sketch, "E322", {"start": v(26.32, -17.47) * mm, "mid": v(26.27, -17.69) * mm, "end": v(26.37, -17.88) * mm});
            skArc(sketch, "E323", {"start": v(26.32, -17.47) * mm, "mid": v(26.53, -17.15) * mm, "end": v(26.74, -16.82) * mm});
            skLineSegment(sketch, "E324", {"start": v(29.42, -16.6) * mm, "end": v(28.74, -15.68) * mm});
            skLineSegment(sketch, "E325", {"start": v(28.74, -15.68) * mm, "end": v(28.02, -15.17) * mm});
            skArc(sketch, "E326", {"start": v(27.93, -14.77) * mm, "mid": v(27.9, -14.98) * mm, "end": v(28.02, -15.17) * mm});
            skArc(sketch, "E327", {"start": v(27.93, -14.77) * mm, "mid": v(28.1, -14.42) * mm, "end": v(28.28, -14.08) * mm});
            skLineSegment(sketch, "E328", {"start": v(30.92, -13.58) * mm, "end": v(30.15, -12.74) * mm});
            skLineSegment(sketch, "E329", {"start": v(30.15, -12.74) * mm, "end": v(29.4, -12.3) * mm});
            skArc(sketch, "E330", {"start": v(29.26, -11.91) * mm, "mid": v(29.25, -12.13) * mm, "end": v(29.4, -12.3) * mm});
            skArc(sketch, "E331", {"start": v(29.26, -11.91) * mm, "mid": v(29.4, -11.55) * mm, "end": v(29.54, -11.2) * mm});
            skLineSegment(sketch, "E332", {"start": v(32.12, -10.44) * mm, "end": v(31.27, -9.67) * mm});
            skLineSegment(sketch, "E333", {"start": v(31.27, -9.67) * mm, "end": v(30.47, -9.31) * mm});
            skArc(sketch, "E334", {"start": v(30.3, -8.94) * mm, "mid": v(30.31, -9.16) * mm, "end": v(30.47, -9.31) * mm});
            skArc(sketch, "E335", {"start": v(30.3, -8.94) * mm, "mid": v(30.4, -8.57) * mm, "end": v(30.5, -8.2) * mm});
            skLineSegment(sketch, "E336", {"start": v(33, -7.19) * mm, "end": v(32.08, -6.5) * mm});
            skLineSegment(sketch, "E337", {"start": v(32.08, -6.5) * mm, "end": v(31.24, -6.23) * mm});
            skArc(sketch, "E338", {"start": v(31.04, -5.88) * mm, "mid": v(31.07, -6.1) * mm, "end": v(31.24, -6.23) * mm});
            skArc(sketch, "E339", {"start": v(31.04, -5.88) * mm, "mid": v(31.1, -5.5) * mm, "end": v(31.17, -5.12) * mm});
            skLineSegment(sketch, "E340", {"start": v(33.55, -3.87) * mm, "end": v(32.56, -3.28) * mm});
            skLineSegment(sketch, "E341", {"start": v(32.56, -3.28) * mm, "end": v(31.7, -3.1) * mm});
            skArc(sketch, "E342", {"start": v(31.47, -2.76) * mm, "mid": v(31.52, -2.97) * mm, "end": v(31.7, -3.1) * mm});
            skArc(sketch, "E343", {"start": v(31.47, -2.76) * mm, "mid": v(31.5, -2.37) * mm, "end": v(31.52, -1.99) * mm});
            skLineSegment(sketch, "E344", {"start": v(33.76, -0.5) * mm, "end": v(32.73, -0.02) * mm});
            skLineSegment(sketch, "E345", {"start": v(32.73, -0.02) * mm, "end": v(31.86, 0.08) * mm});
            skArc(sketch, "E346", {"start": v(31.58, 0.39) * mm, "mid": v(31.66, 0.18) * mm, "end": v(31.86, 0.08) * mm});
            skArc(sketch, "E347", {"start": v(31.58, 0.39) * mm, "mid": v(31.58, 0.77) * mm, "end": v(31.56, 1.16) * mm});
            skLineSegment(sketch, "E348", {"start": v(33.65, 2.86) * mm, "end": v(32.57, 3.23) * mm});
            skLineSegment(sketch, "E349", {"start": v(32.57, 3.23) * mm, "end": v(31.69, 3.25) * mm});
            skArc(sketch, "E350", {"start": v(31.39, 3.53) * mm, "mid": v(31.49, 3.33) * mm, "end": v(31.69, 3.25) * mm});
            skLineSegment(sketch, "E351", {"start": v(33.2, 6.2) * mm, "end": v(32.08, 6.46) * mm});
            skLineSegment(sketch, "E352", {"start": v(32.08, 6.46) * mm, "end": v(31.2, 6.4) * mm});
            skArc(sketch, "E353", {"start": v(30.88, 6.64) * mm, "mid": v(31, 6.45) * mm, "end": v(31.2, 6.4) * mm});
            skLineSegment(sketch, "E354", {"start": v(32.4, 9.47) * mm, "end": v(31.28, 9.62) * mm});
            skLineSegment(sketch, "E355", {"start": v(31.28, 9.62) * mm, "end": v(30.41, 9.47) * mm});
            skArc(sketch, "E356", {"start": v(30.06, 9.68) * mm, "mid": v(30.2, 9.5) * mm, "end": v(30.41, 9.47) * mm});
            skLineSegment(sketch, "E357", {"start": v(31.3, 12.65) * mm, "end": v(30.16, 12.69) * mm});
            skLineSegment(sketch, "E358", {"start": v(30.16, 12.69) * mm, "end": v(29.32, 12.45) * mm});
            skArc(sketch, "E359", {"start": v(28.95, 12.62) * mm, "mid": v(29.1, 12.47) * mm, "end": v(29.32, 12.45) * mm});
            skLineSegment(sketch, "E360", {"start": v(29.89, 15.7) * mm, "end": v(28.75, 15.63) * mm});
            skLineSegment(sketch, "E361", {"start": v(28.75, 15.63) * mm, "end": v(27.93, 15.3) * mm});
            skArc(sketch, "E362", {"start": v(27.55, 15.44) * mm, "mid": v(27.71, 15.3) * mm, "end": v(27.93, 15.3) * mm});
            skLineSegment(sketch, "E363", {"start": v(28.18, 18.6) * mm, "end": v(27.05, 18.41) * mm});
            skLineSegment(sketch, "E364", {"start": v(27.05, 18.41) * mm, "end": v(26.27, 18.01) * mm});
            skArc(sketch, "E365", {"start": v(25.87, 18.1) * mm, "mid": v(26.05, 17.98) * mm, "end": v(26.27, 18.01) * mm});
            skLineSegment(sketch, "E366", {"start": v(26.18, 21.31) * mm, "end": v(25.08, 21.02) * mm});
            skLineSegment(sketch, "E367", {"start": v(25.08, 21.02) * mm, "end": v(24.34, 20.54) * mm});
            skArc(sketch, "E368", {"start": v(23.94, 20.6) * mm, "mid": v(24.13, 20.49) * mm, "end": v(24.34, 20.54) * mm});
            skLineSegment(sketch, "E369", {"start": v(23.93, 23.81) * mm, "end": v(22.86, 23.4) * mm});
            skLineSegment(sketch, "E370", {"start": v(22.86, 23.4) * mm, "end": v(22.18, 22.86) * mm});
            skArc(sketch, "E371", {"start": v(21.77, 22.88) * mm, "mid": v(21.97, 22.79) * mm, "end": v(22.18, 22.86) * mm});
            skLineSegment(sketch, "E372", {"start": v(21.44, 26.08) * mm, "end": v(20.41, 25.57) * mm});
            skLineSegment(sketch, "E373", {"start": v(20.41, 25.57) * mm, "end": v(19.79, 24.95) * mm});
            skArc(sketch, "E374", {"start": v(19.38, 24.93) * mm, "mid": v(19.59, 24.86) * mm, "end": v(19.79, 24.95) * mm});
            skLineSegment(sketch, "E375", {"start": v(18.73, 28.08) * mm, "end": v(17.77, 27.47) * mm});
            skLineSegment(sketch, "E376", {"start": v(17.77, 27.47) * mm, "end": v(17.2, 26.8) * mm});
            skArc(sketch, "E377", {"start": v(16.8, 26.73) * mm, "mid": v(17.01, 26.7) * mm, "end": v(17.2, 26.8) * mm});
            skLineSegment(sketch, "E378", {"start": v(15.84, 29.8) * mm, "end": v(14.94, 29.1) * mm});
            skLineSegment(sketch, "E379", {"start": v(14.94, 29.1) * mm, "end": v(14.45, 28.38) * mm});
            skArc(sketch, "E380", {"start": v(14.05, 28.27) * mm, "mid": v(14.27, 28.25) * mm, "end": v(14.45, 28.38) * mm});
            skLineSegment(sketch, "E381", {"start": v(12.8, 31.24) * mm, "end": v(11.97, 30.45) * mm});
            skLineSegment(sketch, "E382", {"start": v(11.97, 30.45) * mm, "end": v(11.55, 29.68) * mm});
            skArc(sketch, "E383", {"start": v(11.17, 29.53) * mm, "mid": v(11.39, 29.53) * mm, "end": v(11.55, 29.68) * mm});
            skLineSegment(sketch, "E384", {"start": v(9.62, 32.35) * mm, "end": v(8.87, 31.49) * mm});
            skLineSegment(sketch, "E385", {"start": v(8.87, 31.49) * mm, "end": v(8.54, 30.68) * mm});
            skArc(sketch, "E386", {"start": v(8.17, 30.5) * mm, "mid": v(8.39, 30.52) * mm, "end": v(8.54, 30.68) * mm});
            skLineSegment(sketch, "E387", {"start": v(6.35, 33.15) * mm, "end": v(5.7, 32.22) * mm});
            skLineSegment(sketch, "E388", {"start": v(5.7, 32.22) * mm, "end": v(5.44, 31.38) * mm});
            skArc(sketch, "E389", {"start": v(5.1, 31.16) * mm, "mid": v(5.3, 31.2) * mm, "end": v(5.44, 31.38) * mm});
            skLineSegment(sketch, "E390", {"start": v(3.02, 33.62) * mm, "end": v(2.46, 32.62) * mm});
            skLineSegment(sketch, "E391", {"start": v(2.46, 32.62) * mm, "end": v(2.29, 31.76) * mm});
            skArc(sketch, "E392", {"start": v(1.96, 31.51) * mm, "mid": v(2.17, 31.58) * mm, "end": v(2.29, 31.76) * mm});
            skLineSegment(sketch, "E393", {"start": v(-0.35, 33.75) * mm, "end": v(-0.8, 32.7) * mm});
            skLineSegment(sketch, "E394", {"start": v(-0.8, 32.7) * mm, "end": v(-0.89, 31.83) * mm});
            skArc(sketch, "E395", {"start": v(-1.19, 31.55) * mm, "mid": v(-0.98, 31.63) * mm, "end": v(-0.89, 31.83) * mm});
            skLineSegment(sketch, "E396", {"start": v(-3.7, 33.55) * mm, "end": v(-4.06, 32.46) * mm});
            skLineSegment(sketch, "E397", {"start": v(-4.06, 32.46) * mm, "end": v(-4.05, 31.59) * mm});
            skArc(sketch, "E398", {"start": v(-4.32, 31.27) * mm, "mid": v(-4.13, 31.38) * mm, "end": v(-4.05, 31.59) * mm});
            skLineSegment(sketch, "E399", {"start": v(-7.03, 33.01) * mm, "end": v(-7.27, 31.9) * mm});
            skLineSegment(sketch, "E400", {"start": v(-7.27, 31.9) * mm, "end": v(-7.18, 31.02) * mm});
            skArc(sketch, "E401", {"start": v(-7.42, 30.69) * mm, "mid": v(-7.24, 30.81) * mm, "end": v(-7.18, 31.02) * mm});
            skLineSegment(sketch, "E402", {"start": v(-10.28, 32.15) * mm, "end": v(-10.41, 31.01) * mm});
            skLineSegment(sketch, "E403", {"start": v(-10.41, 31.01) * mm, "end": v(-10.24, 30.16) * mm});
            skArc(sketch, "E404", {"start": v(-10.44, 29.8) * mm, "mid": v(-10.27, 29.94) * mm, "end": v(-10.24, 30.16) * mm});
            skLineSegment(sketch, "E405", {"start": v(-13.44, 30.97) * mm, "end": v(-13.45, 29.82) * mm});
            skLineSegment(sketch, "E406", {"start": v(-13.45, 29.82) * mm, "end": v(-13.19, 28.99) * mm});
            skArc(sketch, "E407", {"start": v(-13.35, 28.61) * mm, "mid": v(-13.2, 28.77) * mm, "end": v(-13.19, 28.99) * mm});
            skLineSegment(sketch, "E408", {"start": v(-16.45, 29.47) * mm, "end": v(-16.35, 28.34) * mm});
            skLineSegment(sketch, "E409", {"start": v(-16.35, 28.34) * mm, "end": v(-16.01, 27.53) * mm});
            skArc(sketch, "E410", {"start": v(-16.14, 27.14) * mm, "mid": v(-16, 27.3) * mm, "end": v(-16.01, 27.53) * mm});
            skLineSegment(sketch, "E411", {"start": v(-19.3, 27.7) * mm, "end": v(-19.1, 26.57) * mm});
            skLineSegment(sketch, "E412", {"start": v(-19.1, 26.57) * mm, "end": v(-18.67, 25.8) * mm});
            skArc(sketch, "E413", {"start": v(-18.76, 25.4) * mm, "mid": v(-18.64, 25.58) * mm, "end": v(-18.67, 25.8) * mm});
            skLineSegment(sketch, "E414", {"start": v(-21.97, 25.63) * mm, "end": v(-21.65, 24.53) * mm});
            skLineSegment(sketch, "E415", {"start": v(-21.65, 24.53) * mm, "end": v(-21.15, 23.81) * mm});
            skArc(sketch, "E416", {"start": v(-21.2, 23.4) * mm, "mid": v(-21.1, 23.6) * mm, "end": v(-21.15, 23.81) * mm});
            skLineSegment(sketch, "E417", {"start": v(-24.41, 23.32) * mm, "end": v(-23.98, 22.26) * mm});
            skLineSegment(sketch, "E418", {"start": v(-23.98, 22.26) * mm, "end": v(-23.42, 21.59) * mm});
            skArc(sketch, "E419", {"start": v(-23.42, 21.18) * mm, "mid": v(-23.34, 21.38) * mm, "end": v(-23.42, 21.59) * mm});
            skLineSegment(sketch, "E420", {"start": v(-26.62, 20.77) * mm, "end": v(-26.08, 19.76) * mm});
            skLineSegment(sketch, "E421", {"start": v(-26.08, 19.76) * mm, "end": v(-25.45, 19.15) * mm});
            skArc(sketch, "E422", {"start": v(-25.42, 18.74) * mm, "mid": v(-25.36, 18.95) * mm, "end": v(-25.45, 19.15) * mm});
            skLineSegment(sketch, "E423", {"start": v(-28.55, 18.02) * mm, "end": v(-27.92, 17.06) * mm});
            skLineSegment(sketch, "E424", {"start": v(-27.92, 17.06) * mm, "end": v(-27.23, 16.52) * mm});
            skArc(sketch, "E425", {"start": v(-27.16, 16.11) * mm, "mid": v(-27.12, 16.33) * mm, "end": v(-27.23, 16.52) * mm});
            skLineSegment(sketch, "E426", {"start": v(-30.2, 15.08) * mm, "end": v(-29.48, 14.2) * mm});
            skLineSegment(sketch, "E427", {"start": v(-29.48, 14.2) * mm, "end": v(-28.74, 13.72) * mm});
            skArc(sketch, "E428", {"start": v(-28.63, 13.33) * mm, "mid": v(-28.61, 13.55) * mm, "end": v(-28.74, 13.72) * mm});
            skLineSegment(sketch, "E429", {"start": v(-31.56, 12) * mm, "end": v(-30.75, 11.2) * mm});
            skLineSegment(sketch, "E430", {"start": v(-30.75, 11.2) * mm, "end": v(-29.97, 10.8) * mm});
            skArc(sketch, "E431", {"start": v(-29.81, 10.41) * mm, "mid": v(-29.82, 10.63) * mm, "end": v(-29.97, 10.8) * mm});
            skLineSegment(sketch, "E432", {"start": v(-32.6, 8.8) * mm, "end": v(-31.71, 8.07) * mm});
            skLineSegment(sketch, "E433", {"start": v(-31.71, 8.07) * mm, "end": v(-30.9, 7.76) * mm});
            skArc(sketch, "E434", {"start": v(-30.7, 7.4) * mm, "mid": v(-30.73, 7.61) * mm, "end": v(-30.9, 7.76) * mm});
            skLineSegment(sketch, "E435", {"start": v(-33.31, 5.5) * mm, "end": v(-32.36, 4.88) * mm});
            skLineSegment(sketch, "E436", {"start": v(-32.36, 4.88) * mm, "end": v(-31.52, 4.64) * mm});
            skArc(sketch, "E437", {"start": v(-31.29, 4.3) * mm, "mid": v(-31.34, 4.51) * mm, "end": v(-31.52, 4.64) * mm});
            skLineSegment(sketch, "E438", {"start": v(-33.7, 2.16) * mm, "end": v(-32.69, 1.63) * mm});
            skLineSegment(sketch, "E439", {"start": v(-32.69, 1.63) * mm, "end": v(-31.82, 1.48) * mm});
            skArc(sketch, "E440", {"start": v(-31.56, 1.16) * mm, "mid": v(-31.63, 1.37) * mm, "end": v(-31.82, 1.48) * mm});
            skArc(sketch, "E441", {"start": v(-33.76, -0.5) * mm, "mid": v(-33.76, -0.86) * mm, "end": v(-33.75, -1.2) * mm});
            skArc(sketch, "E442", {"start": v(-33.55, -3.87) * mm, "mid": v(-33.5, -4.21) * mm, "end": v(-33.46, -4.56) * mm});
            skArc(sketch, "E443", {"start": v(-33.65, 2.86) * mm, "mid": v(-33.67, 2.51) * mm, "end": v(-33.7, 2.16) * mm});
            skArc(sketch, "E444", {"start": v(-33, -7.19) * mm, "mid": v(-32.92, -7.53) * mm, "end": v(-32.84, -7.86) * mm});
            skArc(sketch, "E445", {"start": v(-33.2, 6.2) * mm, "mid": v(-33.25, 5.85) * mm, "end": v(-33.31, 5.5) * mm});
            skArc(sketch, "E446", {"start": v(-32.12, -10.44) * mm, "mid": v(-32, -10.77) * mm, "end": v(-31.9, -11.1) * mm});
            skArc(sketch, "E447", {"start": v(-32.4, 9.47) * mm, "mid": v(-32.5, 9.13) * mm, "end": v(-32.6, 8.8) * mm});
            skArc(sketch, "E448", {"start": v(-30.92, -13.58) * mm, "mid": v(-30.78, -13.9) * mm, "end": v(-30.64, -14.22) * mm});
            skArc(sketch, "E449", {"start": v(-31.3, 12.65) * mm, "mid": v(-31.43, 12.32) * mm, "end": v(-31.56, 12) * mm});
            skArc(sketch, "E450", {"start": v(-29.42, -16.6) * mm, "mid": v(-29.24, -16.9) * mm, "end": v(-29.07, -17.2) * mm});
            skArc(sketch, "E451", {"start": v(-29.89, 15.7) * mm, "mid": v(-30.05, 15.4) * mm, "end": v(-30.2, 15.08) * mm});
            skArc(sketch, "E452", {"start": v(-27.62, -19.44) * mm, "mid": v(-27.42, -19.72) * mm, "end": v(-27.21, -20) * mm});
            skArc(sketch, "E453", {"start": v(-28.18, 18.6) * mm, "mid": v(-28.37, 18.3) * mm, "end": v(-28.55, 18.02) * mm});
            skArc(sketch, "E454", {"start": v(-25.55, -22.1) * mm, "mid": v(-25.32, -22.36) * mm, "end": v(-25.09, -22.62) * mm});
            skArc(sketch, "E455", {"start": v(-26.18, 21.31) * mm, "mid": v(-26.4, 21.04) * mm, "end": v(-26.62, 20.77) * mm});
            skArc(sketch, "E456", {"start": v(-23.22, -24.53) * mm, "mid": v(-22.97, -24.77) * mm, "end": v(-22.71, -25) * mm});
            skArc(sketch, "E457", {"start": v(-23.93, 23.81) * mm, "mid": v(-24.17, 23.56) * mm, "end": v(-24.41, 23.32) * mm});
            skArc(sketch, "E458", {"start": v(-20.66, -26.72) * mm, "mid": v(-20.39, -26.93) * mm, "end": v(-20.11, -27.14) * mm});
            skArc(sketch, "E459", {"start": v(-21.44, 26.08) * mm, "mid": v(-21.7, 25.85) * mm, "end": v(-21.97, 25.63) * mm});
            skArc(sketch, "E460", {"start": v(-17.9, -28.64) * mm, "mid": v(-17.6, -28.83) * mm, "end": v(-17.31, -29) * mm});
            skArc(sketch, "E461", {"start": v(-18.73, 28.08) * mm, "mid": v(-19.02, 27.89) * mm, "end": v(-19.3, 27.7) * mm});
            skArc(sketch, "E462", {"start": v(-14.96, -30.28) * mm, "mid": v(-14.65, -30.44) * mm, "end": v(-14.34, -30.59) * mm});
            skArc(sketch, "E463", {"start": v(-15.84, 29.8) * mm, "mid": v(-16.15, 29.64) * mm, "end": v(-16.45, 29.47) * mm});
            skArc(sketch, "E464", {"start": v(-11.87, -31.62) * mm, "mid": v(-11.55, -31.74) * mm, "end": v(-11.22, -31.86) * mm});
            skArc(sketch, "E465", {"start": v(-12.8, 31.24) * mm, "mid": v(-13.12, 31.1) * mm, "end": v(-13.44, 30.97) * mm});
            skArc(sketch, "E466", {"start": v(-8.67, -32.65) * mm, "mid": v(-8.33, -32.74) * mm, "end": v(-8, -32.82) * mm});
            skArc(sketch, "E467", {"start": v(-9.62, 32.35) * mm, "mid": v(-9.95, 32.25) * mm, "end": v(-10.28, 32.15) * mm});
            skArc(sketch, "E468", {"start": v(-5.38, -33.35) * mm, "mid": v(-5.03, -33.4) * mm, "end": v(-4.69, -33.45) * mm});
            skArc(sketch, "E469", {"start": v(-6.35, 33.15) * mm, "mid": v(-6.7, 33.08) * mm, "end": v(-7.03, 33.01) * mm});
            skArc(sketch, "E470", {"start": v(-2.03, -33.72) * mm, "mid": v(-1.68, -33.74) * mm, "end": v(-1.34, -33.75) * mm});
            skArc(sketch, "E471", {"start": v(-3.02, 33.62) * mm, "mid": v(-3.36, 33.59) * mm, "end": v(-3.7, 33.55) * mm});
            skArc(sketch, "E472", {"start": v(1.34, -33.75) * mm, "mid": v(1.68, -33.74) * mm, "end": v(2.03, -33.72) * mm});
            skArc(sketch, "E473", {"start": v(0.35, 33.75) * mm, "mid": v(0, 33.75) * mm, "end": v(-0.35, 33.75) * mm});
            skArc(sketch, "E474", {"start": v(4.69, -33.45) * mm, "mid": v(5.03, -33.4) * mm, "end": v(5.38, -33.35) * mm});
            skArc(sketch, "E475", {"start": v(3.7, 33.55) * mm, "mid": v(3.36, 33.59) * mm, "end": v(3.02, 33.62) * mm});
            skArc(sketch, "E476", {"start": v(8, -32.82) * mm, "mid": v(8.33, -32.74) * mm, "end": v(8.67, -32.65) * mm});
            skArc(sketch, "E477", {"start": v(7.03, 33.01) * mm, "mid": v(6.7, 33.08) * mm, "end": v(6.35, 33.15) * mm});
            skArc(sketch, "E478", {"start": v(11.22, -31.86) * mm, "mid": v(11.55, -31.74) * mm, "end": v(11.87, -31.62) * mm});
            skArc(sketch, "E479", {"start": v(10.28, 32.15) * mm, "mid": v(9.95, 32.25) * mm, "end": v(9.62, 32.35) * mm});
            skArc(sketch, "E480", {"start": v(14.34, -30.59) * mm, "mid": v(14.65, -30.44) * mm, "end": v(14.96, -30.28) * mm});
            skArc(sketch, "E481", {"start": v(13.44, 30.97) * mm, "mid": v(13.12, 31.1) * mm, "end": v(12.8, 31.24) * mm});
            skArc(sketch, "E482", {"start": v(17.31, -29) * mm, "mid": v(17.6, -28.83) * mm, "end": v(17.9, -28.64) * mm});
            skArc(sketch, "E483", {"start": v(16.45, 29.47) * mm, "mid": v(16.15, 29.64) * mm, "end": v(15.84, 29.8) * mm});
            skArc(sketch, "E484", {"start": v(20.11, -27.14) * mm, "mid": v(20.39, -26.93) * mm, "end": v(20.66, -26.72) * mm});
            skArc(sketch, "E485", {"start": v(19.3, 27.7) * mm, "mid": v(19.02, 27.89) * mm, "end": v(18.73, 28.08) * mm});
            skArc(sketch, "E486", {"start": v(22.71, -25) * mm, "mid": v(22.97, -24.77) * mm, "end": v(23.22, -24.53) * mm});
            skArc(sketch, "E487", {"start": v(21.97, 25.63) * mm, "mid": v(21.7, 25.85) * mm, "end": v(21.44, 26.08) * mm});
            skArc(sketch, "E488", {"start": v(25.09, -22.62) * mm, "mid": v(25.32, -22.36) * mm, "end": v(25.55, -22.1) * mm});
            skArc(sketch, "E489", {"start": v(24.41, 23.32) * mm, "mid": v(24.17, 23.56) * mm, "end": v(23.93, 23.81) * mm});
            skArc(sketch, "E490", {"start": v(27.21, -20) * mm, "mid": v(27.42, -19.72) * mm, "end": v(27.62, -19.44) * mm});
            skArc(sketch, "E491", {"start": v(26.62, 20.77) * mm, "mid": v(26.4, 21.04) * mm, "end": v(26.18, 21.31) * mm});
            skArc(sketch, "E492", {"start": v(29.07, -17.2) * mm, "mid": v(29.24, -16.9) * mm, "end": v(29.42, -16.6) * mm});
            skArc(sketch, "E493", {"start": v(28.55, 18.02) * mm, "mid": v(28.37, 18.3) * mm, "end": v(28.18, 18.6) * mm});
            skArc(sketch, "E494", {"start": v(30.64, -14.22) * mm, "mid": v(30.78, -13.9) * mm, "end": v(30.92, -13.58) * mm});
            skArc(sketch, "E495", {"start": v(30.2, 15.08) * mm, "mid": v(30.05, 15.4) * mm, "end": v(29.89, 15.7) * mm});
            skArc(sketch, "E496", {"start": v(31.9, -11.1) * mm, "mid": v(32, -10.77) * mm, "end": v(32.12, -10.44) * mm});
            skArc(sketch, "E497", {"start": v(31.56, 12) * mm, "mid": v(31.43, 12.32) * mm, "end": v(31.3, 12.65) * mm});
            skArc(sketch, "E498", {"start": v(32.84, -7.86) * mm, "mid": v(-30.7, 14.05) * mm, "end": v(27.4, -19.76) * mm});
            skArc(sketch, "E499", {"start": v(32.6, 8.8) * mm, "mid": v(32.5, 9.13) * mm, "end": v(32.4, 9.47) * mm});
            skArc(sketch, "E500", {"start": v(33.46, -4.56) * mm, "mid": v(33.5, -4.21) * mm, "end": v(33.55, -3.87) * mm});
            skArc(sketch, "E501", {"start": v(33.31, 5.5) * mm, "mid": v(33.25, 5.85) * mm, "end": v(33.2, 6.2) * mm});
            skArc(sketch, "E502", {"start": v(33.75, -1.2) * mm, "mid": v(33.76, -0.86) * mm, "end": v(33.76, -0.5) * mm});
            skArc(sketch, "E503", {"start": v(33.7, 2.16) * mm, "mid": v(33.67, 2.51) * mm, "end": v(33.65, 2.86) * mm});
            skCircle(sketch, "E504", {"center": v(0, 0) * mm, "radius": 36.96 * mm});
            skCircle(sketch, "E505", {"center": v(0, 0) * mm, "radius": 9 * mm});
            skCircle(sketch, "E506", {"center": v(0, 0) * mm, "radius": 5 * mm});
            skLineSegment(sketch, "E507", {"start": v(0, 0) * mm, "end": v(36.96, 0) * mm});
            skLineSegment(sketch, "E508", {"start": v(0, 36.96) * mm, "end": v(0, -36.96) * mm});
            skLineSegment(sketch, "E509", {"start": v(0, 0) * mm, "end": v(-36.96, -0.02) * mm});
            skLineSegment(sketch, "E510", {"start": v(0, 0) * mm, "end": v(31.24, -19.76) * mm});
            skLineSegment(sketch, "E511", {"start": v(31.24, -19.76) * mm, "end": v(-31.24, 19.76) * mm});
            skSolve(sketch);
        }
        {
            var Q0;
            Q0=makeQuery(id+"F0.imprint","IMPRINT",FACE,{"disambiguationData":[TD([[makeQuery(id+"F0.imprint","IMPRINT",EDGE,{"derivedFrom":sQuery(id+"F0.wireOp",EDGE,"E0")}),-1.0]])]});
            var Q1;
            {var subQ8=sQuery(id+"F0.wireOp",EDGE,"E4");Q1=makeQuery(id+"F0.imprint","IMPRINT",FACE,{"disambiguationData":[TD([[makeQuery(id+"F0.imprint","IMPRINT",EDGE,{"derivedFrom":subQ8}),-1.0]])]});}
            var Q2;
            Q2=makeQuery(id+"F0.imprint","IMPRINT",FACE,{"disambiguationData":[TD([[makeQuery(id+"F0.imprint","IMPRINT",EDGE,{"derivedFrom":sQuery(id+"F0.wireOp",EDGE,"E46")}),-1.0]])]});
            var Q3;
            Q3=makeQuery(id+"F0.imprint","IMPRINT",FACE,{"disambiguationData":[TD([[makeQuery(id+"F0.imprint","IMPRINT",EDGE,{"derivedFrom":sQuery(id+"F0.wireOp",EDGE,"E116")}),-1.0]])]});
            var Q4;
            {var subQ27=sQuery(id+"F0.wireOp",EDGE,"E178");Q4=makeQuery(id+"F0.imprint","IMPRINT",FACE,{"disambiguationData":[TD([[makeQuery(id+"F0.imprint","IMPRINT",EDGE,{"derivedFrom":subQ27}),1.0]])]});}
            var Q5;
            {var subQ40=sQuery(id+"F0.wireOp",EDGE,"E108");Q5=makeQuery(id+"F0.imprint","IMPRINT",FACE,{"disambiguationData":[TD([[makeQuery(id+"F0.imprint","IMPRINT",EDGE,{"derivedFrom":subQ40}),1.0]])]});}
            var Q6;
            {var subQ3=sQuery(id+"F0.wireOp",EDGE,"E505");var subQ5=sQuery(id+"F0.wireOp",EDGE,"E508");var subQ7=makeQuery(id+"F0.imprint","INTERSECT",VERTEX,{"disambiguationData":[OD(0.0)],"derivedFrom":[subQ3,subQ5]});Q6=makeQuery(id+"F0.imprint","IMPRINT",FACE,{"disambiguationData":[TD([[makeQuery(id+"F0.imprint","IMPRINT",EDGE,{"disambiguationData":[TD([[subQ7,-1.0]])],"derivedFrom":subQ3}),1.0]])]});}
            var Q7;
            {var subQ0=sQuery(id+"F0.wireOp",EDGE,"E508");var subQ3=sQuery(id+"F0.wireOp",EDGE,"E505");var subQ4=makeQuery(id+"F0.imprint","INTERSECT",VERTEX,{"disambiguationData":[OD(0.0)],"derivedFrom":[subQ3,subQ0]});Q7=makeQuery(id+"F0.imprint","IMPRINT",FACE,{"disambiguationData":[TD([[makeQuery(id+"F0.imprint","IMPRINT",EDGE,{"disambiguationData":[TD([[subQ4,1.0]])],"derivedFrom":subQ3}),1.0]])]});}
            var Q8;
            {var subQ3=sQuery(id+"F0.wireOp",EDGE,"E505");var subQ5=sQuery(id+"F0.wireOp",EDGE,"E507");var subQ7=makeQuery(id+"F0.imprint","INTERSECT",VERTEX,{"derivedFrom":[subQ3,subQ5]});Q8=makeQuery(id+"F0.imprint","IMPRINT",FACE,{"disambiguationData":[TD([[makeQuery(id+"F0.imprint","IMPRINT",EDGE,{"disambiguationData":[TD([[subQ7,1.0]])],"derivedFrom":subQ3}),1.0]])]});}
            var Q9;
            {var subQ3=sQuery(id+"F0.wireOp",EDGE,"E505");var subQ5=sQuery(id+"F0.wireOp",EDGE,"E508");var subQ7=makeQuery(id+"F0.imprint","INTERSECT",VERTEX,{"disambiguationData":[OD(1.0)],"derivedFrom":[subQ3,subQ5]});Q9=makeQuery(id+"F0.imprint","IMPRINT",FACE,{"disambiguationData":[TD([[makeQuery(id+"F0.imprint","IMPRINT",EDGE,{"disambiguationData":[TD([[subQ7,-1.0]])],"derivedFrom":subQ3}),1.0]])]});}
            var Q10;
            {var subQ0=sQuery(id+"F0.wireOp",EDGE,"E509");var subQ3=sQuery(id+"F0.wireOp",EDGE,"E505");var subQ4=makeQuery(id+"F0.imprint","INTERSECT",VERTEX,{"derivedFrom":[subQ3,subQ0]});Q10=makeQuery(id+"F0.imprint","IMPRINT",FACE,{"disambiguationData":[TD([[makeQuery(id+"F0.imprint","IMPRINT",EDGE,{"disambiguationData":[TD([[subQ4,-1.0]])],"derivedFrom":subQ3}),1.0]])]});}
            var Q11;
            {var subQ0=sQuery(id+"F0.wireOp",EDGE,"E511");var subQ3=sQuery(id+"F0.wireOp",EDGE,"E505");var subQ4=makeQuery(id+"F0.imprint","INTERSECT",VERTEX,{"disambiguationData":[OD(0.0)],"derivedFrom":[subQ3,subQ0]});Q11=makeQuery(id+"F0.imprint","IMPRINT",FACE,{"disambiguationData":[TD([[makeQuery(id+"F0.imprint","IMPRINT",EDGE,{"disambiguationData":[TD([[subQ4,-1.0]])],"derivedFrom":subQ3}),1.0]])]});}
            extrude(context, id + "F1", {"entities" : qUnion([Q0, Q1, Q2, Q3, Q4, Q5, Q6, Q7, Q8, Q9, Q10, Q11]), "depth" : 5 * mm});
        }
        {
            var Q0;
            {var subQ0=sQuery(id+"F0.wireOp",EDGE,"E511");var subQ3=sQuery(id+"F0.wireOp",EDGE,"E505");var subQ4=makeQuery(id+"F0.imprint","INTERSECT",VERTEX,{"disambiguationData":[OD(0.0)],"derivedFrom":[subQ3,subQ0]});Q0=makeQuery(id+"F0.imprint","IMPRINT",FACE,{"disambiguationData":[TD([[makeQuery(id+"F0.imprint","IMPRINT",EDGE,{"disambiguationData":[TD([[subQ4,-1.0]])],"derivedFrom":subQ3}),1.0]])]});}
            var Q1;
            {var subQ0=sQuery(id+"F0.wireOp",EDGE,"E509");var subQ3=sQuery(id+"F0.wireOp",EDGE,"E505");var subQ4=makeQuery(id+"F0.imprint","INTERSECT",VERTEX,{"derivedFrom":[subQ3,subQ0]});Q1=makeQuery(id+"F0.imprint","IMPRINT",FACE,{"disambiguationData":[TD([[makeQuery(id+"F0.imprint","IMPRINT",EDGE,{"disambiguationData":[TD([[subQ4,-1.0]])],"derivedFrom":subQ3}),1.0]])]});}
            var Q2;
            {var subQ3=sQuery(id+"F0.wireOp",EDGE,"E505");var subQ5=sQuery(id+"F0.wireOp",EDGE,"E508");var subQ7=makeQuery(id+"F0.imprint","INTERSECT",VERTEX,{"disambiguationData":[OD(0.0)],"derivedFrom":[subQ3,subQ5]});Q2=makeQuery(id+"F0.imprint","IMPRINT",FACE,{"disambiguationData":[TD([[makeQuery(id+"F0.imprint","IMPRINT",EDGE,{"disambiguationData":[TD([[subQ7,-1.0]])],"derivedFrom":subQ3}),1.0]])]});}
            var Q3;
            {var subQ0=sQuery(id+"F0.wireOp",EDGE,"E508");var subQ3=sQuery(id+"F0.wireOp",EDGE,"E505");var subQ4=makeQuery(id+"F0.imprint","INTERSECT",VERTEX,{"disambiguationData":[OD(0.0)],"derivedFrom":[subQ3,subQ0]});Q3=makeQuery(id+"F0.imprint","IMPRINT",FACE,{"disambiguationData":[TD([[makeQuery(id+"F0.imprint","IMPRINT",EDGE,{"disambiguationData":[TD([[subQ4,1.0]])],"derivedFrom":subQ3}),1.0]])]});}
            var Q4;
            {var subQ3=sQuery(id+"F0.wireOp",EDGE,"E505");var subQ5=sQuery(id+"F0.wireOp",EDGE,"E508");var subQ7=makeQuery(id+"F0.imprint","INTERSECT",VERTEX,{"disambiguationData":[OD(1.0)],"derivedFrom":[subQ3,subQ5]});Q4=makeQuery(id+"F0.imprint","IMPRINT",FACE,{"disambiguationData":[TD([[makeQuery(id+"F0.imprint","IMPRINT",EDGE,{"disambiguationData":[TD([[subQ7,-1.0]])],"derivedFrom":subQ3}),1.0]])]});}
            var Q5;
            {var subQ3=sQuery(id+"F0.wireOp",EDGE,"E505");var subQ5=sQuery(id+"F0.wireOp",EDGE,"E507");var subQ7=makeQuery(id+"F0.imprint","INTERSECT",VERTEX,{"derivedFrom":[subQ3,subQ5]});Q5=makeQuery(id+"F0.imprint","IMPRINT",FACE,{"disambiguationData":[TD([[makeQuery(id+"F0.imprint","IMPRINT",EDGE,{"disambiguationData":[TD([[subQ7,1.0]])],"derivedFrom":subQ3}),1.0]])]});}
            extrude(context, id + "F2", {"entities" : qUnion([Q0, Q1, Q2, Q3, Q4, Q5]), "operationType" : NewBodyOperationType.ADD, "depth" : 25 * mm});
        }
        {
            var Q0;
            Q0=makeQuery(id+"F2.opExtrude","CAP_FACE",FACE,{"disambiguationData":[OSD([sQuery(id+"F0.wireOp",EDGE,"E505"),sQuery(id+"F0.wireOp",EDGE,"E506")])],"isStart":false});
            var sketch = newSketch(context, id + "F3", { "sketchPlane" : qUnion([Q0])});
            skCircle(sketch, "E512.cCircle", {"center": v(0, 0) * mm, "radius": 9 * mm, "construction": true});
            skLineSegment(sketch, "E512.0", {"start": v(0, -9) * mm, "end": v(-7.8, -4.5) * mm});
            skLineSegment(sketch, "E512.1", {"start": v(-7.8, -4.5) * mm, "end": v(-7.8, 4.5) * mm});
            skLineSegment(sketch, "E512.2", {"start": v(-7.8, 4.5) * mm, "end": v(0, 9) * mm});
            skLineSegment(sketch, "E512.3", {"start": v(0, 9) * mm, "end": v(7.8, 4.5) * mm});
            skLineSegment(sketch, "E512.4", {"start": v(7.8, 4.5) * mm, "end": v(7.8, -4.5) * mm});
            skLineSegment(sketch, "E512.5", {"start": v(7.8, -4.5) * mm, "end": v(0, -9) * mm});
            skSolve(sketch);
        }
        {
            var Q0;
            {var subQ1=sQuery(id+"F3.wireOp",EDGE,"E512.3");Q0=makeQuery(id+"F3.imprint","IMPRINT",FACE,{"disambiguationData":[TD([[makeQuery(id+"F3.imprint","IMPRINT",EDGE,{"derivedFrom":subQ1}),1.0]])]});}
            var Q1;
            {var subQ1=sQuery(id+"F3.wireOp",EDGE,"E512.4");Q1=makeQuery(id+"F3.imprint","IMPRINT",FACE,{"disambiguationData":[TD([[makeQuery(id+"F3.imprint","IMPRINT",EDGE,{"derivedFrom":subQ1}),1.0]])]});}
            var Q2;
            {var subQ1=sQuery(id+"F3.wireOp",EDGE,"E512.5");Q2=makeQuery(id+"F3.imprint","IMPRINT",FACE,{"disambiguationData":[TD([[makeQuery(id+"F3.imprint","IMPRINT",EDGE,{"derivedFrom":subQ1}),1.0]])]});}
            var Q3;
            {var subQ1=sQuery(id+"F3.wireOp",EDGE,"E512.0");Q3=makeQuery(id+"F3.imprint","IMPRINT",FACE,{"disambiguationData":[TD([[makeQuery(id+"F3.imprint","IMPRINT",EDGE,{"derivedFrom":subQ1}),1.0]])]});}
            var Q4;
            {var subQ1=sQuery(id+"F3.wireOp",EDGE,"E512.1");Q4=makeQuery(id+"F3.imprint","IMPRINT",FACE,{"disambiguationData":[TD([[makeQuery(id+"F3.imprint","IMPRINT",EDGE,{"derivedFrom":subQ1}),1.0]])]});}
            var Q5;
            {var subQ1=sQuery(id+"F3.wireOp",EDGE,"E512.2");Q5=makeQuery(id+"F3.imprint","IMPRINT",FACE,{"disambiguationData":[TD([[makeQuery(id+"F3.imprint","IMPRINT",EDGE,{"derivedFrom":subQ1}),1.0]])]});}
            extrude(context, id + "F4", {"entities" : qUnion([Q0, Q1, Q2, Q3, Q4, Q5]), "operationType" : NewBodyOperationType.REMOVE, "oppositeDirection" : true, "depth" : 8 * mm});
        }
        {
            var Q0;
            Q0=makeQuery(id+"F1.opExtrude","CAP_FACE",FACE,{"disambiguationData":[OSD([sQuery(id+"F0.wireOp",EDGE,"E0"),sQuery(id+"F0.wireOp",EDGE,"E1"),sQuery(id+"F0.wireOp",EDGE,"E2"),sQuery(id+"F0.wireOp",EDGE,"E3"),sQuery(id+"F0.wireOp",EDGE,"E4"),sQuery(id+"F0.wireOp",EDGE,"E5"),sQuery(id+"F0.wireOp",EDGE,"E6"),sQuery(id+"F0.wireOp",EDGE,"E7"),sQuery(id+"F0.wireOp",EDGE,"E8"),sQuery(id+"F0.wireOp",EDGE,"E9"),sQuery(id+"F0.wireOp",EDGE,"E10"),sQuery(id+"F0.wireOp",EDGE,"E11"),sQuery(id+"F0.wireOp",EDGE,"E12"),sQuery(id+"F0.wireOp",EDGE,"E13"),sQuery(id+"F0.wireOp",EDGE,"E14"),sQuery(id+"F0.wireOp",EDGE,"E15"),sQuery(id+"F0.wireOp",EDGE,"E16"),sQuery(id+"F0.wireOp",EDGE,"E17"),sQuery(id+"F0.wireOp",EDGE,"E18"),sQuery(id+"F0.wireOp",EDGE,"E19"),sQuery(id+"F0.wireOp",EDGE,"E20"),sQuery(id+"F0.wireOp",EDGE,"E21"),sQuery(id+"F0.wireOp",EDGE,"E22"),sQuery(id+"F0.wireOp",EDGE,"E23"),sQuery(id+"F0.wireOp",EDGE,"E24"),sQuery(id+"F0.wireOp",EDGE,"E25"),sQuery(id+"F0.wireOp",EDGE,"E26"),sQuery(id+"F0.wireOp",EDGE,"E27"),sQuery(id+"F0.wireOp",EDGE,"E28"),sQuery(id+"F0.wireOp",EDGE,"E29"),sQuery(id+"F0.wireOp",EDGE,"E30"),sQuery(id+"F0.wireOp",EDGE,"E31"),sQuery(id+"F0.wireOp",EDGE,"E32"),sQuery(id+"F0.wireOp",EDGE,"E33"),sQuery(id+"F0.wireOp",EDGE,"E34"),sQuery(id+"F0.wireOp",EDGE,"E35"),sQuery(id+"F0.wireOp",EDGE,"E36"),sQuery(id+"F0.wireOp",EDGE,"E37"),sQuery(id+"F0.wireOp",EDGE,"E38"),sQuery(id+"F0.wireOp",EDGE,"E39"),sQuery(id+"F0.wireOp",EDGE,"E40"),sQuery(id+"F0.wireOp",EDGE,"E41"),sQuery(id+"F0.wireOp",EDGE,"E42"),sQuery(id+"F0.wireOp",EDGE,"E43"),sQuery(id+"F0.wireOp",EDGE,"E44"),sQuery(id+"F0.wireOp",EDGE,"E45"),sQuery(id+"F0.wireOp",EDGE,"E46"),sQuery(id+"F0.wireOp",EDGE,"E47"),sQuery(id+"F0.wireOp",EDGE,"E48"),sQuery(id+"F0.wireOp",EDGE,"E49"),sQuery(id+"F0.wireOp",EDGE,"E50"),sQuery(id+"F0.wireOp",EDGE,"E51"),sQuery(id+"F0.wireOp",EDGE,"E52"),sQuery(id+"F0.wireOp",EDGE,"E53"),sQuery(id+"F0.wireOp",EDGE,"E54"),sQuery(id+"F0.wireOp",EDGE,"E55"),sQuery(id+"F0.wireOp",EDGE,"E56"),sQuery(id+"F0.wireOp",EDGE,"E57"),sQuery(id+"F0.wireOp",EDGE,"E58"),sQuery(id+"F0.wireOp",EDGE,"E59"),sQuery(id+"F0.wireOp",EDGE,"E60"),sQuery(id+"F0.wireOp",EDGE,"E61"),sQuery(id+"F0.wireOp",EDGE,"E62"),sQuery(id+"F0.wireOp",EDGE,"E63"),sQuery(id+"F0.wireOp",EDGE,"E64"),sQuery(id+"F0.wireOp",EDGE,"E65"),sQuery(id+"F0.wireOp",EDGE,"E66"),sQuery(id+"F0.wireOp",EDGE,"E67"),sQuery(id+"F0.wireOp",EDGE,"E68"),sQuery(id+"F0.wireOp",EDGE,"E69"),sQuery(id+"F0.wireOp",EDGE,"E70"),sQuery(id+"F0.wireOp",EDGE,"E71"),sQuery(id+"F0.wireOp",EDGE,"E72"),sQuery(id+"F0.wireOp",EDGE,"E73"),sQuery(id+"F0.wireOp",EDGE,"E74"),sQuery(id+"F0.wireOp",EDGE,"E75"),sQuery(id+"F0.wireOp",EDGE,"E76"),sQuery(id+"F0.wireOp",EDGE,"E77"),sQuery(id+"F0.wireOp",EDGE,"E78"),sQuery(id+"F0.wireOp",EDGE,"E79"),sQuery(id+"F0.wireOp",EDGE,"E80"),sQuery(id+"F0.wireOp",EDGE,"E81"),sQuery(id+"F0.wireOp",EDGE,"E82"),sQuery(id+"F0.wireOp",EDGE,"E83"),sQuery(id+"F0.wireOp",EDGE,"E84"),sQuery(id+"F0.wireOp",EDGE,"E85"),sQuery(id+"F0.wireOp",EDGE,"E86"),sQuery(id+"F0.wireOp",EDGE,"E87"),sQuery(id+"F0.wireOp",EDGE,"E88"),sQuery(id+"F0.wireOp",EDGE,"E89"),sQuery(id+"F0.wireOp",EDGE,"E90"),sQuery(id+"F0.wireOp",EDGE,"E91"),sQuery(id+"F0.wireOp",EDGE,"E92"),sQuery(id+"F0.wireOp",EDGE,"E93"),sQuery(id+"F0.wireOp",EDGE,"E94"),sQuery(id+"F0.wireOp",EDGE,"E95"),sQuery(id+"F0.wireOp",EDGE,"E96"),sQuery(id+"F0.wireOp",EDGE,"E97"),sQuery(id+"F0.wireOp",EDGE,"E98"),sQuery(id+"F0.wireOp",EDGE,"E99"),sQuery(id+"F0.wireOp",EDGE,"E100"),sQuery(id+"F0.wireOp",EDGE,"E101"),sQuery(id+"F0.wireOp",EDGE,"E102"),sQuery(id+"F0.wireOp",EDGE,"E103"),sQuery(id+"F0.wireOp",EDGE,"E104"),sQuery(id+"F0.wireOp",EDGE,"E105"),sQuery(id+"F0.wireOp",EDGE,"E106"),sQuery(id+"F0.wireOp",EDGE,"E107"),sQuery(id+"F0.wireOp",EDGE,"E108"),sQuery(id+"F0.wireOp",EDGE,"E109"),sQuery(id+"F0.wireOp",EDGE,"E110"),sQuery(id+"F0.wireOp",EDGE,"E111"),sQuery(id+"F0.wireOp",EDGE,"E112"),sQuery(id+"F0.wireOp",EDGE,"E113"),sQuery(id+"F0.wireOp",EDGE,"E114"),sQuery(id+"F0.wireOp",EDGE,"E115"),sQuery(id+"F0.wireOp",EDGE,"E116"),sQuery(id+"F0.wireOp",EDGE,"E117"),sQuery(id+"F0.wireOp",EDGE,"E118"),sQuery(id+"F0.wireOp",EDGE,"E119"),sQuery(id+"F0.wireOp",EDGE,"E120"),sQuery(id+"F0.wireOp",EDGE,"E121"),sQuery(id+"F0.wireOp",EDGE,"E122"),sQuery(id+"F0.wireOp",EDGE,"E123"),sQuery(id+"F0.wireOp",EDGE,"E124"),sQuery(id+"F0.wireOp",EDGE,"E125"),sQuery(id+"F0.wireOp",EDGE,"E126"),sQuery(id+"F0.wireOp",EDGE,"E127"),sQuery(id+"F0.wireOp",EDGE,"E128"),sQuery(id+"F0.wireOp",EDGE,"E129"),sQuery(id+"F0.wireOp",EDGE,"E130"),sQuery(id+"F0.wireOp",EDGE,"E131"),sQuery(id+"F0.wireOp",EDGE,"E132"),sQuery(id+"F0.wireOp",EDGE,"E133"),sQuery(id+"F0.wireOp",EDGE,"E134"),sQuery(id+"F0.wireOp",EDGE,"E135"),sQuery(id+"F0.wireOp",EDGE,"E136"),sQuery(id+"F0.wireOp",EDGE,"E137"),sQuery(id+"F0.wireOp",EDGE,"E138"),sQuery(id+"F0.wireOp",EDGE,"E139"),sQuery(id+"F0.wireOp",EDGE,"E140"),sQuery(id+"F0.wireOp",EDGE,"E141"),sQuery(id+"F0.wireOp",EDGE,"E142"),sQuery(id+"F0.wireOp",EDGE,"E143"),sQuery(id+"F0.wireOp",EDGE,"E144"),sQuery(id+"F0.wireOp",EDGE,"E145"),sQuery(id+"F0.wireOp",EDGE,"E146"),sQuery(id+"F0.wireOp",EDGE,"E147"),sQuery(id+"F0.wireOp",EDGE,"E148"),sQuery(id+"F0.wireOp",EDGE,"E149"),sQuery(id+"F0.wireOp",EDGE,"E150"),sQuery(id+"F0.wireOp",EDGE,"E151"),sQuery(id+"F0.wireOp",EDGE,"E152"),sQuery(id+"F0.wireOp",EDGE,"E153"),sQuery(id+"F0.wireOp",EDGE,"E154"),sQuery(id+"F0.wireOp",EDGE,"E155"),sQuery(id+"F0.wireOp",EDGE,"E156"),sQuery(id+"F0.wireOp",EDGE,"E157"),sQuery(id+"F0.wireOp",EDGE,"E158"),sQuery(id+"F0.wireOp",EDGE,"E159"),sQuery(id+"F0.wireOp",EDGE,"E160"),sQuery(id+"F0.wireOp",EDGE,"E161"),sQuery(id+"F0.wireOp",EDGE,"E162"),sQuery(id+"F0.wireOp",EDGE,"E163"),sQuery(id+"F0.wireOp",EDGE,"E164"),sQuery(id+"F0.wireOp",EDGE,"E165"),sQuery(id+"F0.wireOp",EDGE,"E166"),sQuery(id+"F0.wireOp",EDGE,"E167"),sQuery(id+"F0.wireOp",EDGE,"E168"),sQuery(id+"F0.wireOp",EDGE,"E169"),sQuery(id+"F0.wireOp",EDGE,"E170"),sQuery(id+"F0.wireOp",EDGE,"E171"),sQuery(id+"F0.wireOp",EDGE,"E172"),sQuery(id+"F0.wireOp",EDGE,"E173"),sQuery(id+"F0.wireOp",EDGE,"E174"),sQuery(id+"F0.wireOp",EDGE,"E175"),sQuery(id+"F0.wireOp",EDGE,"E176"),sQuery(id+"F0.wireOp",EDGE,"E177"),sQuery(id+"F0.wireOp",EDGE,"E178"),sQuery(id+"F0.wireOp",EDGE,"E179"),sQuery(id+"F0.wireOp",EDGE,"E180"),sQuery(id+"F0.wireOp",EDGE,"E181"),sQuery(id+"F0.wireOp",EDGE,"E182"),sQuery(id+"F0.wireOp",EDGE,"E183"),sQuery(id+"F0.wireOp",EDGE,"E184"),sQuery(id+"F0.wireOp",EDGE,"E185"),sQuery(id+"F0.wireOp",EDGE,"E186"),sQuery(id+"F0.wireOp",EDGE,"E187"),sQuery(id+"F0.wireOp",EDGE,"E188"),sQuery(id+"F0.wireOp",EDGE,"E189"),sQuery(id+"F0.wireOp",EDGE,"E190"),sQuery(id+"F0.wireOp",EDGE,"E191"),sQuery(id+"F0.wireOp",EDGE,"E192"),sQuery(id+"F0.wireOp",EDGE,"E193"),sQuery(id+"F0.wireOp",EDGE,"E194"),sQuery(id+"F0.wireOp",EDGE,"E195"),sQuery(id+"F0.wireOp",EDGE,"E196"),sQuery(id+"F0.wireOp",EDGE,"E197"),sQuery(id+"F0.wireOp",EDGE,"E198"),sQuery(id+"F0.wireOp",EDGE,"E199"),sQuery(id+"F0.wireOp",EDGE,"E200"),sQuery(id+"F0.wireOp",EDGE,"E201"),sQuery(id+"F0.wireOp",EDGE,"E202"),sQuery(id+"F0.wireOp",EDGE,"E203"),sQuery(id+"F0.wireOp",EDGE,"E204"),sQuery(id+"F0.wireOp",EDGE,"E205"),sQuery(id+"F0.wireOp",EDGE,"E206"),sQuery(id+"F0.wireOp",EDGE,"E207"),sQuery(id+"F0.wireOp",EDGE,"E208"),sQuery(id+"F0.wireOp",EDGE,"E209"),sQuery(id+"F0.wireOp",EDGE,"E210"),sQuery(id+"F0.wireOp",EDGE,"E211"),sQuery(id+"F0.wireOp",EDGE,"E212"),sQuery(id+"F0.wireOp",EDGE,"E213"),sQuery(id+"F0.wireOp",EDGE,"E214"),sQuery(id+"F0.wireOp",EDGE,"E215"),sQuery(id+"F0.wireOp",EDGE,"E216"),sQuery(id+"F0.wireOp",EDGE,"E217"),sQuery(id+"F0.wireOp",EDGE,"E218"),sQuery(id+"F0.wireOp",EDGE,"E219"),sQuery(id+"F0.wireOp",EDGE,"E220"),sQuery(id+"F0.wireOp",EDGE,"E221"),sQuery(id+"F0.wireOp",EDGE,"E222"),sQuery(id+"F0.wireOp",EDGE,"E223"),sQuery(id+"F0.wireOp",EDGE,"E224"),sQuery(id+"F0.wireOp",EDGE,"E225"),sQuery(id+"F0.wireOp",EDGE,"E226"),sQuery(id+"F0.wireOp",EDGE,"E227"),sQuery(id+"F0.wireOp",EDGE,"E228"),sQuery(id+"F0.wireOp",EDGE,"E229"),sQuery(id+"F0.wireOp",EDGE,"E230"),sQuery(id+"F0.wireOp",EDGE,"E231"),sQuery(id+"F0.wireOp",EDGE,"E232"),sQuery(id+"F0.wireOp",EDGE,"E233"),sQuery(id+"F0.wireOp",EDGE,"E234"),sQuery(id+"F0.wireOp",EDGE,"E235"),sQuery(id+"F0.wireOp",EDGE,"E236"),sQuery(id+"F0.wireOp",EDGE,"E237"),sQuery(id+"F0.wireOp",EDGE,"E238"),sQuery(id+"F0.wireOp",EDGE,"E239"),sQuery(id+"F0.wireOp",EDGE,"E240"),sQuery(id+"F0.wireOp",EDGE,"E241"),sQuery(id+"F0.wireOp",EDGE,"E242"),sQuery(id+"F0.wireOp",EDGE,"E243"),sQuery(id+"F0.wireOp",EDGE,"E244"),sQuery(id+"F0.wireOp",EDGE,"E245"),sQuery(id+"F0.wireOp",EDGE,"E246"),sQuery(id+"F0.wireOp",EDGE,"E247"),sQuery(id+"F0.wireOp",EDGE,"E248"),sQuery(id+"F0.wireOp",EDGE,"E249"),sQuery(id+"F0.wireOp",EDGE,"E250"),sQuery(id+"F0.wireOp",EDGE,"E251"),sQuery(id+"F0.wireOp",EDGE,"E252"),sQuery(id+"F0.wireOp",EDGE,"E253"),sQuery(id+"F0.wireOp",EDGE,"E254"),sQuery(id+"F0.wireOp",EDGE,"E255"),sQuery(id+"F0.wireOp",EDGE,"E256"),sQuery(id+"F0.wireOp",EDGE,"E257"),sQuery(id+"F0.wireOp",EDGE,"E258"),sQuery(id+"F0.wireOp",EDGE,"E259"),sQuery(id+"F0.wireOp",EDGE,"E260"),sQuery(id+"F0.wireOp",EDGE,"E261"),sQuery(id+"F0.wireOp",EDGE,"E262"),sQuery(id+"F0.wireOp",EDGE,"E263"),sQuery(id+"F0.wireOp",EDGE,"E264"),sQuery(id+"F0.wireOp",EDGE,"E265"),sQuery(id+"F0.wireOp",EDGE,"E266"),sQuery(id+"F0.wireOp",EDGE,"E267"),sQuery(id+"F0.wireOp",EDGE,"E268"),sQuery(id+"F0.wireOp",EDGE,"E269"),sQuery(id+"F0.wireOp",EDGE,"E270"),sQuery(id+"F0.wireOp",EDGE,"E271"),sQuery(id+"F0.wireOp",EDGE,"E272"),sQuery(id+"F0.wireOp",EDGE,"E273"),sQuery(id+"F0.wireOp",EDGE,"E274"),sQuery(id+"F0.wireOp",EDGE,"E275"),sQuery(id+"F0.wireOp",EDGE,"E276"),sQuery(id+"F0.wireOp",EDGE,"E277"),sQuery(id+"F0.wireOp",EDGE,"E278"),sQuery(id+"F0.wireOp",EDGE,"E279"),sQuery(id+"F0.wireOp",EDGE,"E280"),sQuery(id+"F0.wireOp",EDGE,"E281"),sQuery(id+"F0.wireOp",EDGE,"E282"),sQuery(id+"F0.wireOp",EDGE,"E283"),sQuery(id+"F0.wireOp",EDGE,"E284"),sQuery(id+"F0.wireOp",EDGE,"E285"),sQuery(id+"F0.wireOp",EDGE,"E286"),sQuery(id+"F0.wireOp",EDGE,"E287"),sQuery(id+"F0.wireOp",EDGE,"E288"),sQuery(id+"F0.wireOp",EDGE,"E289"),sQuery(id+"F0.wireOp",EDGE,"E290"),sQuery(id+"F0.wireOp",EDGE,"E291"),sQuery(id+"F0.wireOp",EDGE,"E292"),sQuery(id+"F0.wireOp",EDGE,"E293"),sQuery(id+"F0.wireOp",EDGE,"E294"),sQuery(id+"F0.wireOp",EDGE,"E295"),sQuery(id+"F0.wireOp",EDGE,"E296"),sQuery(id+"F0.wireOp",EDGE,"E297"),sQuery(id+"F0.wireOp",EDGE,"E298"),sQuery(id+"F0.wireOp",EDGE,"E299"),sQuery(id+"F0.wireOp",EDGE,"E300"),sQuery(id+"F0.wireOp",EDGE,"E301"),sQuery(id+"F0.wireOp",EDGE,"E302"),sQuery(id+"F0.wireOp",EDGE,"E303"),sQuery(id+"F0.wireOp",EDGE,"E304"),sQuery(id+"F0.wireOp",EDGE,"E305"),sQuery(id+"F0.wireOp",EDGE,"E306"),sQuery(id+"F0.wireOp",EDGE,"E307"),sQuery(id+"F0.wireOp",EDGE,"E308"),sQuery(id+"F0.wireOp",EDGE,"E309"),sQuery(id+"F0.wireOp",EDGE,"E310"),sQuery(id+"F0.wireOp",EDGE,"E311"),sQuery(id+"F0.wireOp",EDGE,"E312"),sQuery(id+"F0.wireOp",EDGE,"E313"),sQuery(id+"F0.wireOp",EDGE,"E314"),sQuery(id+"F0.wireOp",EDGE,"E315"),sQuery(id+"F0.wireOp",EDGE,"E316"),sQuery(id+"F0.wireOp",EDGE,"E317"),sQuery(id+"F0.wireOp",EDGE,"E318"),sQuery(id+"F0.wireOp",EDGE,"E319"),sQuery(id+"F0.wireOp",EDGE,"E320"),sQuery(id+"F0.wireOp",EDGE,"E321"),sQuery(id+"F0.wireOp",EDGE,"E322"),sQuery(id+"F0.wireOp",EDGE,"E323"),sQuery(id+"F0.wireOp",EDGE,"E324"),sQuery(id+"F0.wireOp",EDGE,"E325"),sQuery(id+"F0.wireOp",EDGE,"E326"),sQuery(id+"F0.wireOp",EDGE,"E327"),sQuery(id+"F0.wireOp",EDGE,"E328"),sQuery(id+"F0.wireOp",EDGE,"E329"),sQuery(id+"F0.wireOp",EDGE,"E330"),sQuery(id+"F0.wireOp",EDGE,"E331"),sQuery(id+"F0.wireOp",EDGE,"E332"),sQuery(id+"F0.wireOp",EDGE,"E333"),sQuery(id+"F0.wireOp",EDGE,"E334"),sQuery(id+"F0.wireOp",EDGE,"E335"),sQuery(id+"F0.wireOp",EDGE,"E336"),sQuery(id+"F0.wireOp",EDGE,"E337"),sQuery(id+"F0.wireOp",EDGE,"E338"),sQuery(id+"F0.wireOp",EDGE,"E339"),sQuery(id+"F0.wireOp",EDGE,"E340"),sQuery(id+"F0.wireOp",EDGE,"E341"),sQuery(id+"F0.wireOp",EDGE,"E342"),sQuery(id+"F0.wireOp",EDGE,"E343"),sQuery(id+"F0.wireOp",EDGE,"E344"),sQuery(id+"F0.wireOp",EDGE,"E345"),sQuery(id+"F0.wireOp",EDGE,"E346"),sQuery(id+"F0.wireOp",EDGE,"E347"),sQuery(id+"F0.wireOp",EDGE,"E348"),sQuery(id+"F0.wireOp",EDGE,"E349"),sQuery(id+"F0.wireOp",EDGE,"E350"),sQuery(id+"F0.wireOp",EDGE,"E351"),sQuery(id+"F0.wireOp",EDGE,"E352"),sQuery(id+"F0.wireOp",EDGE,"E353"),sQuery(id+"F0.wireOp",EDGE,"E354"),sQuery(id+"F0.wireOp",EDGE,"E355"),sQuery(id+"F0.wireOp",EDGE,"E356"),sQuery(id+"F0.wireOp",EDGE,"E357"),sQuery(id+"F0.wireOp",EDGE,"E358"),sQuery(id+"F0.wireOp",EDGE,"E359"),sQuery(id+"F0.wireOp",EDGE,"E360"),sQuery(id+"F0.wireOp",EDGE,"E361"),sQuery(id+"F0.wireOp",EDGE,"E362"),sQuery(id+"F0.wireOp",EDGE,"E363"),sQuery(id+"F0.wireOp",EDGE,"E364"),sQuery(id+"F0.wireOp",EDGE,"E365"),sQuery(id+"F0.wireOp",EDGE,"E366"),sQuery(id+"F0.wireOp",EDGE,"E367"),sQuery(id+"F0.wireOp",EDGE,"E368"),sQuery(id+"F0.wireOp",EDGE,"E369"),sQuery(id+"F0.wireOp",EDGE,"E370"),sQuery(id+"F0.wireOp",EDGE,"E371"),sQuery(id+"F0.wireOp",EDGE,"E372"),sQuery(id+"F0.wireOp",EDGE,"E373"),sQuery(id+"F0.wireOp",EDGE,"E374"),sQuery(id+"F0.wireOp",EDGE,"E375"),sQuery(id+"F0.wireOp",EDGE,"E376"),sQuery(id+"F0.wireOp",EDGE,"E377"),sQuery(id+"F0.wireOp",EDGE,"E378"),sQuery(id+"F0.wireOp",EDGE,"E379"),sQuery(id+"F0.wireOp",EDGE,"E380"),sQuery(id+"F0.wireOp",EDGE,"E381"),sQuery(id+"F0.wireOp",EDGE,"E382"),sQuery(id+"F0.wireOp",EDGE,"E383"),sQuery(id+"F0.wireOp",EDGE,"E384"),sQuery(id+"F0.wireOp",EDGE,"E385"),sQuery(id+"F0.wireOp",EDGE,"E386"),sQuery(id+"F0.wireOp",EDGE,"E387"),sQuery(id+"F0.wireOp",EDGE,"E388"),sQuery(id+"F0.wireOp",EDGE,"E389"),sQuery(id+"F0.wireOp",EDGE,"E390"),sQuery(id+"F0.wireOp",EDGE,"E391"),sQuery(id+"F0.wireOp",EDGE,"E392"),sQuery(id+"F0.wireOp",EDGE,"E393"),sQuery(id+"F0.wireOp",EDGE,"E394"),sQuery(id+"F0.wireOp",EDGE,"E395"),sQuery(id+"F0.wireOp",EDGE,"E396"),sQuery(id+"F0.wireOp",EDGE,"E397"),sQuery(id+"F0.wireOp",EDGE,"E398"),sQuery(id+"F0.wireOp",EDGE,"E399"),sQuery(id+"F0.wireOp",EDGE,"E400"),sQuery(id+"F0.wireOp",EDGE,"E401"),sQuery(id+"F0.wireOp",EDGE,"E402"),sQuery(id+"F0.wireOp",EDGE,"E403"),sQuery(id+"F0.wireOp",EDGE,"E404"),sQuery(id+"F0.wireOp",EDGE,"E405"),sQuery(id+"F0.wireOp",EDGE,"E406"),sQuery(id+"F0.wireOp",EDGE,"E407"),sQuery(id+"F0.wireOp",EDGE,"E408"),sQuery(id+"F0.wireOp",EDGE,"E409"),sQuery(id+"F0.wireOp",EDGE,"E410"),sQuery(id+"F0.wireOp",EDGE,"E411"),sQuery(id+"F0.wireOp",EDGE,"E412"),sQuery(id+"F0.wireOp",EDGE,"E413"),sQuery(id+"F0.wireOp",EDGE,"E414"),sQuery(id+"F0.wireOp",EDGE,"E415"),sQuery(id+"F0.wireOp",EDGE,"E416"),sQuery(id+"F0.wireOp",EDGE,"E417"),sQuery(id+"F0.wireOp",EDGE,"E418"),sQuery(id+"F0.wireOp",EDGE,"E419"),sQuery(id+"F0.wireOp",EDGE,"E420"),sQuery(id+"F0.wireOp",EDGE,"E421"),sQuery(id+"F0.wireOp",EDGE,"E422"),sQuery(id+"F0.wireOp",EDGE,"E423"),sQuery(id+"F0.wireOp",EDGE,"E424"),sQuery(id+"F0.wireOp",EDGE,"E425"),sQuery(id+"F0.wireOp",EDGE,"E426"),sQuery(id+"F0.wireOp",EDGE,"E427"),sQuery(id+"F0.wireOp",EDGE,"E428"),sQuery(id+"F0.wireOp",EDGE,"E429"),sQuery(id+"F0.wireOp",EDGE,"E430"),sQuery(id+"F0.wireOp",EDGE,"E431"),sQuery(id+"F0.wireOp",EDGE,"E432"),sQuery(id+"F0.wireOp",EDGE,"E433"),sQuery(id+"F0.wireOp",EDGE,"E434"),sQuery(id+"F0.wireOp",EDGE,"E435"),sQuery(id+"F0.wireOp",EDGE,"E436"),sQuery(id+"F0.wireOp",EDGE,"E437"),sQuery(id+"F0.wireOp",EDGE,"E438"),sQuery(id+"F0.wireOp",EDGE,"E439"),sQuery(id+"F0.wireOp",EDGE,"E440"),sQuery(id+"F0.wireOp",EDGE,"E490"),sQuery(id+"F0.wireOp",EDGE,"E492"),sQuery(id+"F0.wireOp",EDGE,"E494"),sQuery(id+"F0.wireOp",EDGE,"E496"),sQuery(id+"F0.wireOp",EDGE,"E498"),sQuery(id+"F0.wireOp",EDGE,"E499"),sQuery(id+"F0.wireOp",EDGE,"E500"),sQuery(id+"F0.wireOp",EDGE,"E501"),sQuery(id+"F0.wireOp",EDGE,"E502"),sQuery(id+"F0.wireOp",EDGE,"E503"),sQuery(id+"F0.wireOp",EDGE,"E506")])],"isStart":false});
            cPlane(context, id + "F5", {"entities" : qUnion([Q0]), "cplaneType" : CPlaneType.OFFSET, "offset" : 12 * mm, "width" : 150 * mm, "height" : 150 * mm});
        }
        {
            var Q0;
            Q0=qCreatedBy(id+"F5.planeOp",FACE);
            var sketch = newSketch(context, id + "F6", { "sketchPlane" : qUnion([Q0])});
            skArc(sketch, "E513", {"start": v(21, -0.33) * mm, "mid": v(21, -0.17) * mm, "end": v(21, 0) * mm});
            skArc(sketch, "E514", {"start": v(0, -5) * mm, "mid": v(5, 0) * mm, "end": v(0, 5) * mm});
            skArc(sketch, "E515", {"start": v(-21, 0) * mm, "mid": v(-21, -0.17) * mm, "end": v(-21, -0.33) * mm});
            skArc(sketch, "E516", {"start": v(18.87, 1.14) * mm, "mid": v(18.84, 1.48) * mm, "end": v(18.81, 1.83) * mm});
            skArc(sketch, "E517", {"start": v(19.04, 2.15) * mm, "mid": v(18.86, 2.03) * mm, "end": v(18.81, 1.83) * mm});
            skLineSegment(sketch, "E518", {"start": v(19.04, 2.15) * mm, "end": v(19.86, 2.36) * mm});
            skArc(sketch, "E519", {"start": v(19.14, -0.86) * mm, "mid": v(18.95, -0.95) * mm, "end": v(18.87, -1.14) * mm});
            skLineSegment(sketch, "E520", {"start": v(19.86, 2.36) * mm, "end": v(20.8, 2.96) * mm});
            skArc(sketch, "E521", {"start": v(18.46, 4.07) * mm, "mid": v(18.38, 4.41) * mm, "end": v(18.3, 4.75) * mm});
            skLineSegment(sketch, "E522", {"start": v(19.14, -0.86) * mm, "end": v(19.98, -0.78) * mm});
            skArc(sketch, "E523", {"start": v(18.46, 5.1) * mm, "mid": v(18.31, 4.96) * mm, "end": v(18.3, 4.75) * mm});
            skLineSegment(sketch, "E524", {"start": v(19.98, -0.78) * mm, "end": v(21, -0.33) * mm});
            skLineSegment(sketch, "E525", {"start": v(18.46, 5.1) * mm, "end": v(19.25, 5.44) * mm});
            skArc(sketch, "E526", {"start": v(18.77, -3.84) * mm, "mid": v(18.57, -3.9) * mm, "end": v(18.46, -4.07) * mm});
            skLineSegment(sketch, "E527", {"start": v(19.25, 5.44) * mm, "end": v(20.07, 6.17) * mm});
            skArc(sketch, "E528", {"start": v(17.6, 6.91) * mm, "mid": v(17.46, 7.23) * mm, "end": v(17.33, 7.55) * mm});
            skLineSegment(sketch, "E529", {"start": v(18.77, -3.84) * mm, "end": v(19.62, -3.9) * mm});
            skArc(sketch, "E530", {"start": v(17.44, 7.93) * mm, "mid": v(17.31, 7.76) * mm, "end": v(17.33, 7.55) * mm});
            skLineSegment(sketch, "E531", {"start": v(19.62, -3.9) * mm, "end": v(20.69, -3.61) * mm});
            skLineSegment(sketch, "E532", {"start": v(17.44, 7.93) * mm, "end": v(18.16, 8.38) * mm});
            skArc(sketch, "E533", {"start": v(17.94, -6.73) * mm, "mid": v(17.73, -6.76) * mm, "end": v(17.6, -6.91) * mm});
            skLineSegment(sketch, "E534", {"start": v(18.16, 8.38) * mm, "end": v(18.86, 9.24) * mm});
            skArc(sketch, "E535", {"start": v(16.3, 9.58) * mm, "mid": v(16.11, 9.88) * mm, "end": v(15.93, 10.17) * mm});
            skLineSegment(sketch, "E536", {"start": v(17.94, -6.73) * mm, "end": v(18.77, -6.91) * mm});
            skArc(sketch, "E537", {"start": v(15.98, 10.56) * mm, "mid": v(15.89, 10.37) * mm, "end": v(15.93, 10.17) * mm});
            skLineSegment(sketch, "E538", {"start": v(18.77, -6.91) * mm, "end": v(19.87, -6.8) * mm});
            skLineSegment(sketch, "E539", {"start": v(15.98, 10.56) * mm, "end": v(16.62, 11.12) * mm});
            skArc(sketch, "E540", {"start": v(16.66, -9.45) * mm, "mid": v(16.45, -9.45) * mm, "end": v(16.3, -9.58) * mm});
            skLineSegment(sketch, "E541", {"start": v(16.62, 11.12) * mm, "end": v(17.18, 12.07) * mm});
            skArc(sketch, "E542", {"start": v(14.6, 12) * mm, "mid": v(14.37, 12.27) * mm, "end": v(14.14, 12.54) * mm});
            skLineSegment(sketch, "E543", {"start": v(16.66, -9.45) * mm, "end": v(17.45, -9.76) * mm});
            skArc(sketch, "E544", {"start": v(14.14, 12.93) * mm, "mid": v(14.07, 12.73) * mm, "end": v(14.14, 12.54) * mm});
            skLineSegment(sketch, "E545", {"start": v(17.45, -9.76) * mm, "end": v(18.56, -9.83) * mm});
            skLineSegment(sketch, "E546", {"start": v(14.14, 12.93) * mm, "end": v(14.68, 13.58) * mm});
            skArc(sketch, "E547", {"start": v(14.98, -11.94) * mm, "mid": v(14.77, -11.9) * mm, "end": v(14.6, -12) * mm});
            skLineSegment(sketch, "E548", {"start": v(14.68, 13.58) * mm, "end": v(15.08, 14.61) * mm});
            skArc(sketch, "E549", {"start": v(12.54, 14.14) * mm, "mid": v(12.27, 14.37) * mm, "end": v(12, 14.6) * mm});
            skLineSegment(sketch, "E550", {"start": v(14.98, -11.94) * mm, "end": v(15.71, -12.37) * mm});
            skArc(sketch, "E551", {"start": v(11.94, 14.98) * mm, "mid": v(11.9, 14.77) * mm, "end": v(12, 14.6) * mm});
            skLineSegment(sketch, "E552", {"start": v(15.71, -12.37) * mm, "end": v(16.8, -12.61) * mm});
            skArc(sketch, "E553", {"start": v(12.93, -14.14) * mm, "mid": v(12.73, -14.07) * mm, "end": v(12.54, -14.14) * mm});
            skLineSegment(sketch, "E554", {"start": v(11.94, 14.98) * mm, "end": v(12.37, 15.71) * mm});
            skLineSegment(sketch, "E555", {"start": v(12.93, -14.14) * mm, "end": v(13.58, -14.68) * mm});
            skLineSegment(sketch, "E556", {"start": v(12.37, 15.71) * mm, "end": v(12.61, 16.8) * mm});
            skArc(sketch, "E557", {"start": v(10.17, 15.93) * mm, "mid": v(9.88, 16.11) * mm, "end": v(9.58, 16.3) * mm});
            skLineSegment(sketch, "E558", {"start": v(13.58, -14.68) * mm, "end": v(14.61, -15.08) * mm});
            skArc(sketch, "E559", {"start": v(9.45, 16.66) * mm, "mid": v(9.45, 16.45) * mm, "end": v(9.58, 16.3) * mm});
            skArc(sketch, "E560", {"start": v(10.56, -15.98) * mm, "mid": v(10.37, -15.89) * mm, "end": v(10.17, -15.93) * mm});
            skLineSegment(sketch, "E561", {"start": v(9.45, 16.66) * mm, "end": v(9.76, 17.45) * mm});
            skLineSegment(sketch, "E562", {"start": v(10.56, -15.98) * mm, "end": v(11.12, -16.62) * mm});
            skLineSegment(sketch, "E563", {"start": v(9.76, 17.45) * mm, "end": v(9.83, 18.56) * mm});
            skArc(sketch, "E564", {"start": v(7.55, 17.33) * mm, "mid": v(7.23, 17.46) * mm, "end": v(6.91, 17.6) * mm});
            skLineSegment(sketch, "E565", {"start": v(11.12, -16.62) * mm, "end": v(12.07, -17.18) * mm});
            skArc(sketch, "E566", {"start": v(6.73, 17.94) * mm, "mid": v(6.76, 17.73) * mm, "end": v(6.91, 17.6) * mm});
            skArc(sketch, "E567", {"start": v(7.93, -17.44) * mm, "mid": v(7.76, -17.31) * mm, "end": v(7.55, -17.33) * mm});
            skLineSegment(sketch, "E568", {"start": v(6.73, 17.94) * mm, "end": v(6.91, 18.77) * mm});
            skLineSegment(sketch, "E569", {"start": v(7.93, -17.44) * mm, "end": v(8.38, -18.16) * mm});
            skLineSegment(sketch, "E570", {"start": v(6.91, 18.77) * mm, "end": v(6.8, 19.87) * mm});
            skArc(sketch, "E571", {"start": v(4.75, 18.3) * mm, "mid": v(4.41, 18.38) * mm, "end": v(4.07, 18.46) * mm});
            skLineSegment(sketch, "E572", {"start": v(8.38, -18.16) * mm, "end": v(9.24, -18.86) * mm});
            skArc(sketch, "E573", {"start": v(3.84, 18.77) * mm, "mid": v(3.9, 18.57) * mm, "end": v(4.07, 18.46) * mm});
            skArc(sketch, "E574", {"start": v(5.1, -18.46) * mm, "mid": v(4.96, -18.31) * mm, "end": v(4.75, -18.3) * mm});
            skLineSegment(sketch, "E575", {"start": v(3.84, 18.77) * mm, "end": v(3.9, 19.62) * mm});
            skLineSegment(sketch, "E576", {"start": v(5.1, -18.46) * mm, "end": v(5.44, -19.25) * mm});
            skLineSegment(sketch, "E577", {"start": v(3.9, 19.62) * mm, "end": v(3.61, 20.69) * mm});
            skArc(sketch, "E578", {"start": v(1.83, 18.81) * mm, "mid": v(1.48, 18.84) * mm, "end": v(1.14, 18.87) * mm});
            skLineSegment(sketch, "E579", {"start": v(5.44, -19.25) * mm, "end": v(6.17, -20.07) * mm});
            skArc(sketch, "E580", {"start": v(0.86, 19.14) * mm, "mid": v(0.95, 18.95) * mm, "end": v(1.14, 18.87) * mm});
            skArc(sketch, "E581", {"start": v(2.15, -19.04) * mm, "mid": v(2.03, -18.86) * mm, "end": v(1.83, -18.81) * mm});
            skLineSegment(sketch, "E582", {"start": v(0.86, 19.14) * mm, "end": v(0.78, 19.98) * mm});
            skArc(sketch, "E583", {"start": v(-1.14, 18.87) * mm, "mid": v(-1.48, 18.84) * mm, "end": v(-1.83, 18.81) * mm});
            skLineSegment(sketch, "E584", {"start": v(2.15, -19.04) * mm, "end": v(2.36, -19.86) * mm});
            skLineSegment(sketch, "E585", {"start": v(0.78, 19.98) * mm, "end": v(0.33, 21) * mm});
            skArc(sketch, "E586", {"start": v(-2.15, 19.04) * mm, "mid": v(-2.03, 18.86) * mm, "end": v(-1.83, 18.81) * mm});
            skLineSegment(sketch, "E587", {"start": v(2.36, -19.86) * mm, "end": v(2.96, -20.8) * mm});
            skArc(sketch, "E588", {"start": v(-0.86, -19.14) * mm, "mid": v(-0.95, -18.95) * mm, "end": v(-1.14, -18.87) * mm});
            skLineSegment(sketch, "E589", {"start": v(-2.15, 19.04) * mm, "end": v(-2.36, 19.86) * mm});
            skLineSegment(sketch, "E590", {"start": v(-0.86, -19.14) * mm, "end": v(-0.78, -19.98) * mm});
            skLineSegment(sketch, "E591", {"start": v(-2.36, 19.86) * mm, "end": v(-2.96, 20.8) * mm});
            skArc(sketch, "E592", {"start": v(-4.07, 18.46) * mm, "mid": v(-4.41, 18.38) * mm, "end": v(-4.75, 18.3) * mm});
            skLineSegment(sketch, "E593", {"start": v(-0.78, -19.98) * mm, "end": v(-0.33, -21) * mm});
            skArc(sketch, "E594", {"start": v(-5.1, 18.46) * mm, "mid": v(-4.96, 18.31) * mm, "end": v(-4.75, 18.3) * mm});
            skArc(sketch, "E595", {"start": v(-3.84, -18.77) * mm, "mid": v(-3.9, -18.57) * mm, "end": v(-4.07, -18.46) * mm});
            skLineSegment(sketch, "E596", {"start": v(-5.1, 18.46) * mm, "end": v(-5.44, 19.25) * mm});
            skLineSegment(sketch, "E597", {"start": v(-3.84, -18.77) * mm, "end": v(-3.9, -19.62) * mm});
            skLineSegment(sketch, "E598", {"start": v(-5.44, 19.25) * mm, "end": v(-6.17, 20.07) * mm});
            skArc(sketch, "E599", {"start": v(-6.91, 17.6) * mm, "mid": v(-7.23, 17.46) * mm, "end": v(-7.55, 17.33) * mm});
            skLineSegment(sketch, "E600", {"start": v(-3.9, -19.62) * mm, "end": v(-3.61, -20.69) * mm});
            skArc(sketch, "E601", {"start": v(-7.93, 17.44) * mm, "mid": v(-7.76, 17.31) * mm, "end": v(-7.55, 17.33) * mm});
            skArc(sketch, "E602", {"start": v(-6.73, -17.94) * mm, "mid": v(-6.76, -17.73) * mm, "end": v(-6.91, -17.6) * mm});
            skLineSegment(sketch, "E603", {"start": v(-7.93, 17.44) * mm, "end": v(-8.38, 18.16) * mm});
            skLineSegment(sketch, "E604", {"start": v(-6.73, -17.94) * mm, "end": v(-6.91, -18.77) * mm});
            skLineSegment(sketch, "E605", {"start": v(-8.38, 18.16) * mm, "end": v(-9.24, 18.86) * mm});
            skArc(sketch, "E606", {"start": v(-9.58, 16.3) * mm, "mid": v(-9.88, 16.11) * mm, "end": v(-10.17, 15.93) * mm});
            skLineSegment(sketch, "E607", {"start": v(-6.91, -18.77) * mm, "end": v(-6.8, -19.87) * mm});
            skArc(sketch, "E608", {"start": v(-10.56, 15.98) * mm, "mid": v(-10.37, 15.89) * mm, "end": v(-10.17, 15.93) * mm});
            skArc(sketch, "E609", {"start": v(-9.45, -16.66) * mm, "mid": v(-9.45, -16.45) * mm, "end": v(-9.58, -16.3) * mm});
            skLineSegment(sketch, "E610", {"start": v(-10.56, 15.98) * mm, "end": v(-11.12, 16.62) * mm});
            skLineSegment(sketch, "E611", {"start": v(-9.45, -16.66) * mm, "end": v(-9.76, -17.45) * mm});
            skLineSegment(sketch, "E612", {"start": v(-11.12, 16.62) * mm, "end": v(-12.07, 17.18) * mm});
            skArc(sketch, "E613", {"start": v(-12, 14.6) * mm, "mid": v(-12.27, 14.37) * mm, "end": v(-12.54, 14.14) * mm});
            skLineSegment(sketch, "E614", {"start": v(-9.76, -17.45) * mm, "end": v(-9.83, -18.56) * mm});
            skArc(sketch, "E615", {"start": v(-12.93, 14.14) * mm, "mid": v(-12.73, 14.07) * mm, "end": v(-12.54, 14.14) * mm});
            skArc(sketch, "E616", {"start": v(-11.94, -14.98) * mm, "mid": v(-11.9, -14.77) * mm, "end": v(-12, -14.6) * mm});
            skLineSegment(sketch, "E617", {"start": v(-12.93, 14.14) * mm, "end": v(-13.58, 14.68) * mm});
            skLineSegment(sketch, "E618", {"start": v(-11.94, -14.98) * mm, "end": v(-12.37, -15.71) * mm});
            skLineSegment(sketch, "E619", {"start": v(-13.58, 14.68) * mm, "end": v(-14.61, 15.08) * mm});
            skArc(sketch, "E620", {"start": v(-14.14, 12.54) * mm, "mid": v(-14.37, 12.27) * mm, "end": v(-14.6, 12) * mm});
            skLineSegment(sketch, "E621", {"start": v(-12.37, -15.71) * mm, "end": v(-12.61, -16.8) * mm});
            skArc(sketch, "E622", {"start": v(-14.98, 11.94) * mm, "mid": v(-14.77, 11.9) * mm, "end": v(-14.6, 12) * mm});
            skArc(sketch, "E623", {"start": v(-14.14, -12.93) * mm, "mid": v(-14.07, -12.73) * mm, "end": v(-14.14, -12.54) * mm});
            skLineSegment(sketch, "E624", {"start": v(-14.98, 11.94) * mm, "end": v(-15.71, 12.37) * mm});
            skLineSegment(sketch, "E625", {"start": v(-14.14, -12.93) * mm, "end": v(-14.68, -13.58) * mm});
            skLineSegment(sketch, "E626", {"start": v(-15.71, 12.37) * mm, "end": v(-16.8, 12.61) * mm});
            skArc(sketch, "E627", {"start": v(-15.93, 10.17) * mm, "mid": v(-16.11, 9.88) * mm, "end": v(-16.3, 9.58) * mm});
            skLineSegment(sketch, "E628", {"start": v(-14.68, -13.58) * mm, "end": v(-15.08, -14.61) * mm});
            skArc(sketch, "E629", {"start": v(-16.66, 9.45) * mm, "mid": v(-16.45, 9.45) * mm, "end": v(-16.3, 9.58) * mm});
            skArc(sketch, "E630", {"start": v(-15.98, -10.56) * mm, "mid": v(-15.89, -10.37) * mm, "end": v(-15.93, -10.17) * mm});
            skLineSegment(sketch, "E631", {"start": v(-16.66, 9.45) * mm, "end": v(-17.45, 9.76) * mm});
            skLineSegment(sketch, "E632", {"start": v(-15.98, -10.56) * mm, "end": v(-16.62, -11.12) * mm});
            skLineSegment(sketch, "E633", {"start": v(-17.45, 9.76) * mm, "end": v(-18.56, 9.83) * mm});
            skArc(sketch, "E634", {"start": v(-17.33, 7.55) * mm, "mid": v(-17.46, 7.23) * mm, "end": v(-17.6, 6.91) * mm});
            skLineSegment(sketch, "E635", {"start": v(-16.62, -11.12) * mm, "end": v(-17.18, -12.07) * mm});
            skArc(sketch, "E636", {"start": v(-17.94, 6.73) * mm, "mid": v(-17.73, 6.76) * mm, "end": v(-17.6, 6.91) * mm});
            skArc(sketch, "E637", {"start": v(-17.44, -7.93) * mm, "mid": v(-17.31, -7.76) * mm, "end": v(-17.33, -7.55) * mm});
            skLineSegment(sketch, "E638", {"start": v(-17.94, 6.73) * mm, "end": v(-18.77, 6.91) * mm});
            skLineSegment(sketch, "E639", {"start": v(-17.44, -7.93) * mm, "end": v(-18.16, -8.38) * mm});
            skLineSegment(sketch, "E640", {"start": v(-18.77, 6.91) * mm, "end": v(-19.87, 6.8) * mm});
            skArc(sketch, "E641", {"start": v(-18.3, 4.75) * mm, "mid": v(-18.38, 4.41) * mm, "end": v(-18.46, 4.07) * mm});
            skLineSegment(sketch, "E642", {"start": v(-18.16, -8.38) * mm, "end": v(-18.86, -9.24) * mm});
            skArc(sketch, "E643", {"start": v(-18.77, 3.84) * mm, "mid": v(-18.57, 3.9) * mm, "end": v(-18.46, 4.07) * mm});
            skArc(sketch, "E644", {"start": v(-18.46, -5.1) * mm, "mid": v(-18.31, -4.96) * mm, "end": v(-18.3, -4.75) * mm});
            skLineSegment(sketch, "E645", {"start": v(-18.77, 3.84) * mm, "end": v(-19.62, 3.9) * mm});
            skLineSegment(sketch, "E646", {"start": v(-18.46, -5.1) * mm, "end": v(-19.25, -5.44) * mm});
            skLineSegment(sketch, "E647", {"start": v(-19.62, 3.9) * mm, "end": v(-20.69, 3.61) * mm});
            skArc(sketch, "E648", {"start": v(-18.81, 1.83) * mm, "mid": v(-18.84, 1.48) * mm, "end": v(-18.87, 1.14) * mm});
            skLineSegment(sketch, "E649", {"start": v(-19.25, -5.44) * mm, "end": v(-20.07, -6.17) * mm});
            skArc(sketch, "E650", {"start": v(-19.14, 0.86) * mm, "mid": v(-18.95, 0.95) * mm, "end": v(-18.87, 1.14) * mm});
            skLineSegment(sketch, "E651", {"start": v(-19.14, 0.86) * mm, "end": v(-19.98, 0.78) * mm});
            skArc(sketch, "E652", {"start": v(-19.04, -2.15) * mm, "mid": v(-18.86, -2.03) * mm, "end": v(-18.81, -1.83) * mm});
            skLineSegment(sketch, "E653", {"start": v(-19.04, -2.15) * mm, "end": v(-19.86, -2.36) * mm});
            skLineSegment(sketch, "E654", {"start": v(-19.98, 0.78) * mm, "end": v(-21, 0.33) * mm});
            skLineSegment(sketch, "E655", {"start": v(-19.86, -2.36) * mm, "end": v(-20.8, -2.96) * mm});
            skLineSegment(sketch, "E656", {"start": v(-21, -0.33) * mm, "end": v(-19.98, -0.78) * mm});
            skLineSegment(sketch, "E657", {"start": v(-19.98, -0.78) * mm, "end": v(-19.14, -0.86) * mm});
            skArc(sketch, "E658", {"start": v(-18.87, -1.14) * mm, "mid": v(-18.95, -0.95) * mm, "end": v(-19.14, -0.86) * mm});
            skArc(sketch, "E659", {"start": v(-18.87, -1.14) * mm, "mid": v(-18.84, -1.48) * mm, "end": v(-18.81, -1.83) * mm});
            skLineSegment(sketch, "E660", {"start": v(-20.69, -3.61) * mm, "end": v(-19.62, -3.9) * mm});
            skLineSegment(sketch, "E661", {"start": v(-19.62, -3.9) * mm, "end": v(-18.77, -3.84) * mm});
            skArc(sketch, "E662", {"start": v(-18.46, -4.07) * mm, "mid": v(-18.57, -3.9) * mm, "end": v(-18.77, -3.84) * mm});
            skArc(sketch, "E663", {"start": v(-18.46, -4.07) * mm, "mid": v(-18.38, -4.41) * mm, "end": v(-18.3, -4.75) * mm});
            skLineSegment(sketch, "E664", {"start": v(-19.87, -6.8) * mm, "end": v(-18.77, -6.91) * mm});
            skLineSegment(sketch, "E665", {"start": v(-18.77, -6.91) * mm, "end": v(-17.94, -6.73) * mm});
            skArc(sketch, "E666", {"start": v(-17.6, -6.91) * mm, "mid": v(-17.73, -6.76) * mm, "end": v(-17.94, -6.73) * mm});
            skArc(sketch, "E667", {"start": v(-17.6, -6.91) * mm, "mid": v(-17.46, -7.23) * mm, "end": v(-17.33, -7.55) * mm});
            skLineSegment(sketch, "E668", {"start": v(-18.56, -9.83) * mm, "end": v(-17.45, -9.76) * mm});
            skLineSegment(sketch, "E669", {"start": v(-17.45, -9.76) * mm, "end": v(-16.66, -9.45) * mm});
            skArc(sketch, "E670", {"start": v(-16.3, -9.58) * mm, "mid": v(-16.45, -9.45) * mm, "end": v(-16.66, -9.45) * mm});
            skArc(sketch, "E671", {"start": v(-16.3, -9.58) * mm, "mid": v(-16.11, -9.88) * mm, "end": v(-15.93, -10.17) * mm});
            skLineSegment(sketch, "E672", {"start": v(-16.8, -12.61) * mm, "end": v(-15.71, -12.37) * mm});
            skLineSegment(sketch, "E673", {"start": v(-15.71, -12.37) * mm, "end": v(-14.98, -11.94) * mm});
            skArc(sketch, "E674", {"start": v(-14.6, -12) * mm, "mid": v(-14.77, -11.9) * mm, "end": v(-14.98, -11.94) * mm});
            skArc(sketch, "E675", {"start": v(-14.6, -12) * mm, "mid": v(-14.37, -12.27) * mm, "end": v(-14.14, -12.54) * mm});
            skLineSegment(sketch, "E676", {"start": v(-14.61, -15.08) * mm, "end": v(-13.58, -14.68) * mm});
            skLineSegment(sketch, "E677", {"start": v(-13.58, -14.68) * mm, "end": v(-12.93, -14.14) * mm});
            skArc(sketch, "E678", {"start": v(-12.54, -14.14) * mm, "mid": v(-12.73, -14.07) * mm, "end": v(-12.93, -14.14) * mm});
            skArc(sketch, "E679", {"start": v(-12.54, -14.14) * mm, "mid": v(-12.27, -14.37) * mm, "end": v(-12, -14.6) * mm});
            skLineSegment(sketch, "E680", {"start": v(-12.07, -17.18) * mm, "end": v(-11.12, -16.62) * mm});
            skLineSegment(sketch, "E681", {"start": v(-11.12, -16.62) * mm, "end": v(-10.56, -15.98) * mm});
            skArc(sketch, "E682", {"start": v(-10.17, -15.93) * mm, "mid": v(-10.37, -15.89) * mm, "end": v(-10.56, -15.98) * mm});
            skArc(sketch, "E683", {"start": v(-10.17, -15.93) * mm, "mid": v(-9.88, -16.11) * mm, "end": v(-9.58, -16.3) * mm});
            skLineSegment(sketch, "E684", {"start": v(-9.24, -18.86) * mm, "end": v(-8.38, -18.16) * mm});
            skLineSegment(sketch, "E685", {"start": v(-8.38, -18.16) * mm, "end": v(-7.93, -17.44) * mm});
            skArc(sketch, "E686", {"start": v(-7.55, -17.33) * mm, "mid": v(-7.76, -17.31) * mm, "end": v(-7.93, -17.44) * mm});
            skArc(sketch, "E687", {"start": v(-7.55, -17.33) * mm, "mid": v(-7.23, -17.46) * mm, "end": v(-6.91, -17.6) * mm});
            skLineSegment(sketch, "E688", {"start": v(-6.17, -20.07) * mm, "end": v(-5.44, -19.25) * mm});
            skLineSegment(sketch, "E689", {"start": v(-5.44, -19.25) * mm, "end": v(-5.1, -18.46) * mm});
            skArc(sketch, "E690", {"start": v(-4.75, -18.3) * mm, "mid": v(-4.96, -18.31) * mm, "end": v(-5.1, -18.46) * mm});
            skArc(sketch, "E691", {"start": v(-4.75, -18.3) * mm, "mid": v(-4.41, -18.38) * mm, "end": v(-4.07, -18.46) * mm});
            skLineSegment(sketch, "E692", {"start": v(-2.96, -20.8) * mm, "end": v(-2.36, -19.86) * mm});
            skLineSegment(sketch, "E693", {"start": v(-2.36, -19.86) * mm, "end": v(-2.15, -19.04) * mm});
            skArc(sketch, "E694", {"start": v(-1.83, -18.81) * mm, "mid": v(-2.03, -18.86) * mm, "end": v(-2.15, -19.04) * mm});
            skArc(sketch, "E695", {"start": v(-1.83, -18.81) * mm, "mid": v(-1.48, -18.84) * mm, "end": v(-1.14, -18.87) * mm});
            skLineSegment(sketch, "E696", {"start": v(0.33, -21) * mm, "end": v(0.78, -19.98) * mm});
            skLineSegment(sketch, "E697", {"start": v(0.78, -19.98) * mm, "end": v(0.86, -19.14) * mm});
            skArc(sketch, "E698", {"start": v(1.14, -18.87) * mm, "mid": v(0.95, -18.95) * mm, "end": v(0.86, -19.14) * mm});
            skArc(sketch, "E699", {"start": v(1.14, -18.87) * mm, "mid": v(1.48, -18.84) * mm, "end": v(1.83, -18.81) * mm});
            skLineSegment(sketch, "E700", {"start": v(3.61, -20.69) * mm, "end": v(3.9, -19.62) * mm});
            skLineSegment(sketch, "E701", {"start": v(3.9, -19.62) * mm, "end": v(3.84, -18.77) * mm});
            skArc(sketch, "E702", {"start": v(4.07, -18.46) * mm, "mid": v(3.9, -18.57) * mm, "end": v(3.84, -18.77) * mm});
            skArc(sketch, "E703", {"start": v(4.07, -18.46) * mm, "mid": v(4.41, -18.38) * mm, "end": v(4.75, -18.3) * mm});
            skLineSegment(sketch, "E704", {"start": v(6.8, -19.87) * mm, "end": v(6.91, -18.77) * mm});
            skLineSegment(sketch, "E705", {"start": v(6.91, -18.77) * mm, "end": v(6.73, -17.94) * mm});
            skArc(sketch, "E706", {"start": v(6.91, -17.6) * mm, "mid": v(6.76, -17.73) * mm, "end": v(6.73, -17.94) * mm});
            skArc(sketch, "E707", {"start": v(6.91, -17.6) * mm, "mid": v(7.23, -17.46) * mm, "end": v(7.55, -17.33) * mm});
            skLineSegment(sketch, "E708", {"start": v(9.83, -18.56) * mm, "end": v(9.76, -17.45) * mm});
            skLineSegment(sketch, "E709", {"start": v(9.76, -17.45) * mm, "end": v(9.45, -16.66) * mm});
            skArc(sketch, "E710", {"start": v(9.58, -16.3) * mm, "mid": v(9.45, -16.45) * mm, "end": v(9.45, -16.66) * mm});
            skArc(sketch, "E711", {"start": v(9.58, -16.3) * mm, "mid": v(9.88, -16.11) * mm, "end": v(10.17, -15.93) * mm});
            skLineSegment(sketch, "E712", {"start": v(12.61, -16.8) * mm, "end": v(12.37, -15.71) * mm});
            skLineSegment(sketch, "E713", {"start": v(12.37, -15.71) * mm, "end": v(11.94, -14.98) * mm});
            skArc(sketch, "E714", {"start": v(12, -14.6) * mm, "mid": v(11.9, -14.77) * mm, "end": v(11.94, -14.98) * mm});
            skArc(sketch, "E715", {"start": v(12, -14.6) * mm, "mid": v(12.27, -14.37) * mm, "end": v(12.54, -14.14) * mm});
            skLineSegment(sketch, "E716", {"start": v(15.08, -14.61) * mm, "end": v(14.68, -13.58) * mm});
            skLineSegment(sketch, "E717", {"start": v(14.68, -13.58) * mm, "end": v(14.14, -12.93) * mm});
            skArc(sketch, "E718", {"start": v(14.14, -12.54) * mm, "mid": v(14.07, -12.73) * mm, "end": v(14.14, -12.93) * mm});
            skArc(sketch, "E719", {"start": v(14.14, -12.54) * mm, "mid": v(14.37, -12.27) * mm, "end": v(14.6, -12) * mm});
            skLineSegment(sketch, "E720", {"start": v(17.18, -12.07) * mm, "end": v(16.62, -11.12) * mm});
            skLineSegment(sketch, "E721", {"start": v(16.62, -11.12) * mm, "end": v(15.98, -10.56) * mm});
            skArc(sketch, "E722", {"start": v(15.93, -10.17) * mm, "mid": v(15.89, -10.37) * mm, "end": v(15.98, -10.56) * mm});
            skArc(sketch, "E723", {"start": v(15.93, -10.17) * mm, "mid": v(16.11, -9.88) * mm, "end": v(16.3, -9.58) * mm});
            skLineSegment(sketch, "E724", {"start": v(18.86, -9.24) * mm, "end": v(18.16, -8.38) * mm});
            skLineSegment(sketch, "E725", {"start": v(18.16, -8.38) * mm, "end": v(17.44, -7.93) * mm});
            skArc(sketch, "E726", {"start": v(17.33, -7.55) * mm, "mid": v(17.31, -7.76) * mm, "end": v(17.44, -7.93) * mm});
            skArc(sketch, "E727", {"start": v(17.33, -7.55) * mm, "mid": v(17.46, -7.23) * mm, "end": v(17.6, -6.91) * mm});
            skLineSegment(sketch, "E728", {"start": v(20.07, -6.17) * mm, "end": v(19.25, -5.44) * mm});
            skLineSegment(sketch, "E729", {"start": v(19.25, -5.44) * mm, "end": v(18.46, -5.1) * mm});
            skArc(sketch, "E730", {"start": v(18.3, -4.75) * mm, "mid": v(18.31, -4.96) * mm, "end": v(18.46, -5.1) * mm});
            skArc(sketch, "E731", {"start": v(18.3, -4.75) * mm, "mid": v(18.38, -4.41) * mm, "end": v(18.46, -4.07) * mm});
            skLineSegment(sketch, "E732", {"start": v(20.8, -2.96) * mm, "end": v(19.86, -2.36) * mm});
            skLineSegment(sketch, "E733", {"start": v(19.86, -2.36) * mm, "end": v(19.04, -2.15) * mm});
            skArc(sketch, "E734", {"start": v(18.81, -1.83) * mm, "mid": v(18.86, -2.03) * mm, "end": v(19.04, -2.15) * mm});
            skArc(sketch, "E735", {"start": v(18.81, -1.83) * mm, "mid": v(18.84, -1.48) * mm, "end": v(18.87, -1.14) * mm});
            skLineSegment(sketch, "E736", {"start": v(21, 0.33) * mm, "end": v(19.98, 0.78) * mm});
            skLineSegment(sketch, "E737", {"start": v(19.98, 0.78) * mm, "end": v(19.14, 0.86) * mm});
            skArc(sketch, "E738", {"start": v(18.87, 1.14) * mm, "mid": v(18.95, 0.95) * mm, "end": v(19.14, 0.86) * mm});
            skLineSegment(sketch, "E739", {"start": v(20.69, 3.61) * mm, "end": v(19.62, 3.9) * mm});
            skLineSegment(sketch, "E740", {"start": v(19.62, 3.9) * mm, "end": v(18.77, 3.84) * mm});
            skArc(sketch, "E741", {"start": v(18.46, 4.07) * mm, "mid": v(18.57, 3.9) * mm, "end": v(18.77, 3.84) * mm});
            skLineSegment(sketch, "E742", {"start": v(19.87, 6.8) * mm, "end": v(18.77, 6.91) * mm});
            skLineSegment(sketch, "E743", {"start": v(18.77, 6.91) * mm, "end": v(17.94, 6.73) * mm});
            skArc(sketch, "E744", {"start": v(17.6, 6.91) * mm, "mid": v(17.73, 6.76) * mm, "end": v(17.94, 6.73) * mm});
            skLineSegment(sketch, "E745", {"start": v(18.56, 9.83) * mm, "end": v(17.45, 9.76) * mm});
            skLineSegment(sketch, "E746", {"start": v(17.45, 9.76) * mm, "end": v(16.66, 9.45) * mm});
            skArc(sketch, "E747", {"start": v(16.3, 9.58) * mm, "mid": v(16.45, 9.45) * mm, "end": v(16.66, 9.45) * mm});
            skLineSegment(sketch, "E748", {"start": v(16.8, 12.61) * mm, "end": v(15.71, 12.37) * mm});
            skLineSegment(sketch, "E749", {"start": v(15.71, 12.37) * mm, "end": v(14.98, 11.94) * mm});
            skArc(sketch, "E750", {"start": v(14.6, 12) * mm, "mid": v(14.77, 11.9) * mm, "end": v(14.98, 11.94) * mm});
            skLineSegment(sketch, "E751", {"start": v(14.61, 15.08) * mm, "end": v(13.58, 14.68) * mm});
            skLineSegment(sketch, "E752", {"start": v(13.58, 14.68) * mm, "end": v(12.93, 14.14) * mm});
            skArc(sketch, "E753", {"start": v(12.54, 14.14) * mm, "mid": v(12.73, 14.07) * mm, "end": v(12.93, 14.14) * mm});
            skLineSegment(sketch, "E754", {"start": v(12.07, 17.18) * mm, "end": v(11.12, 16.62) * mm});
            skLineSegment(sketch, "E755", {"start": v(11.12, 16.62) * mm, "end": v(10.56, 15.98) * mm});
            skArc(sketch, "E756", {"start": v(10.17, 15.93) * mm, "mid": v(10.37, 15.89) * mm, "end": v(10.56, 15.98) * mm});
            skLineSegment(sketch, "E757", {"start": v(9.24, 18.86) * mm, "end": v(8.38, 18.16) * mm});
            skLineSegment(sketch, "E758", {"start": v(8.38, 18.16) * mm, "end": v(7.93, 17.44) * mm});
            skArc(sketch, "E759", {"start": v(7.55, 17.33) * mm, "mid": v(7.76, 17.31) * mm, "end": v(7.93, 17.44) * mm});
            skLineSegment(sketch, "E760", {"start": v(6.17, 20.07) * mm, "end": v(5.44, 19.25) * mm});
            skLineSegment(sketch, "E761", {"start": v(5.44, 19.25) * mm, "end": v(5.1, 18.46) * mm});
            skArc(sketch, "E762", {"start": v(4.75, 18.3) * mm, "mid": v(4.96, 18.31) * mm, "end": v(5.1, 18.46) * mm});
            skLineSegment(sketch, "E763", {"start": v(2.96, 20.8) * mm, "end": v(2.36, 19.86) * mm});
            skLineSegment(sketch, "E764", {"start": v(2.36, 19.86) * mm, "end": v(2.15, 19.04) * mm});
            skArc(sketch, "E765", {"start": v(1.83, 18.81) * mm, "mid": v(2.03, 18.86) * mm, "end": v(2.15, 19.04) * mm});
            skLineSegment(sketch, "E766", {"start": v(-0.33, 21) * mm, "end": v(-0.78, 19.98) * mm});
            skLineSegment(sketch, "E767", {"start": v(-0.78, 19.98) * mm, "end": v(-0.86, 19.14) * mm});
            skArc(sketch, "E768", {"start": v(-1.14, 18.87) * mm, "mid": v(-0.95, 18.95) * mm, "end": v(-0.86, 19.14) * mm});
            skLineSegment(sketch, "E769", {"start": v(-3.61, 20.69) * mm, "end": v(-3.9, 19.62) * mm});
            skLineSegment(sketch, "E770", {"start": v(-3.9, 19.62) * mm, "end": v(-3.84, 18.77) * mm});
            skArc(sketch, "E771", {"start": v(-4.07, 18.46) * mm, "mid": v(-3.9, 18.57) * mm, "end": v(-3.84, 18.77) * mm});
            skLineSegment(sketch, "E772", {"start": v(-6.8, 19.87) * mm, "end": v(-6.91, 18.77) * mm});
            skLineSegment(sketch, "E773", {"start": v(-6.91, 18.77) * mm, "end": v(-6.73, 17.94) * mm});
            skArc(sketch, "E774", {"start": v(-6.91, 17.6) * mm, "mid": v(-6.76, 17.73) * mm, "end": v(-6.73, 17.94) * mm});
            skLineSegment(sketch, "E775", {"start": v(-9.83, 18.56) * mm, "end": v(-9.76, 17.45) * mm});
            skLineSegment(sketch, "E776", {"start": v(-9.76, 17.45) * mm, "end": v(-9.45, 16.66) * mm});
            skArc(sketch, "E777", {"start": v(-9.58, 16.3) * mm, "mid": v(-9.45, 16.45) * mm, "end": v(-9.45, 16.66) * mm});
            skLineSegment(sketch, "E778", {"start": v(-12.61, 16.8) * mm, "end": v(-12.37, 15.71) * mm});
            skLineSegment(sketch, "E779", {"start": v(-12.37, 15.71) * mm, "end": v(-11.94, 14.98) * mm});
            skArc(sketch, "E780", {"start": v(-12, 14.6) * mm, "mid": v(-11.9, 14.77) * mm, "end": v(-11.94, 14.98) * mm});
            skLineSegment(sketch, "E781", {"start": v(-15.08, 14.61) * mm, "end": v(-14.68, 13.58) * mm});
            skLineSegment(sketch, "E782", {"start": v(-14.68, 13.58) * mm, "end": v(-14.14, 12.93) * mm});
            skArc(sketch, "E783", {"start": v(-14.14, 12.54) * mm, "mid": v(-14.07, 12.73) * mm, "end": v(-14.14, 12.93) * mm});
            skLineSegment(sketch, "E784", {"start": v(-17.18, 12.07) * mm, "end": v(-16.62, 11.12) * mm});
            skLineSegment(sketch, "E785", {"start": v(-16.62, 11.12) * mm, "end": v(-15.98, 10.56) * mm});
            skArc(sketch, "E786", {"start": v(-15.93, 10.17) * mm, "mid": v(-15.89, 10.37) * mm, "end": v(-15.98, 10.56) * mm});
            skLineSegment(sketch, "E787", {"start": v(-18.86, 9.24) * mm, "end": v(-18.16, 8.38) * mm});
            skLineSegment(sketch, "E788", {"start": v(-18.16, 8.38) * mm, "end": v(-17.44, 7.93) * mm});
            skArc(sketch, "E789", {"start": v(-17.33, 7.55) * mm, "mid": v(-17.31, 7.76) * mm, "end": v(-17.44, 7.93) * mm});
            skLineSegment(sketch, "E790", {"start": v(-20.07, 6.17) * mm, "end": v(-19.25, 5.44) * mm});
            skLineSegment(sketch, "E791", {"start": v(-19.25, 5.44) * mm, "end": v(-18.46, 5.1) * mm});
            skArc(sketch, "E792", {"start": v(-18.3, 4.75) * mm, "mid": v(-18.31, 4.96) * mm, "end": v(-18.46, 5.1) * mm});
            skLineSegment(sketch, "E793", {"start": v(-20.8, 2.96) * mm, "end": v(-19.86, 2.36) * mm});
            skLineSegment(sketch, "E794", {"start": v(-19.86, 2.36) * mm, "end": v(-19.04, 2.15) * mm});
            skArc(sketch, "E795", {"start": v(-18.81, 1.83) * mm, "mid": v(-18.86, 2.03) * mm, "end": v(-19.04, 2.15) * mm});
            skArc(sketch, "E796", {"start": v(21, 0) * mm, "mid": v(21, 0.17) * mm, "end": v(21, 0.33) * mm});
            skArc(sketch, "E797", {"start": v(20.8, 2.96) * mm, "mid": v(20.74, 3.29) * mm, "end": v(20.69, 3.61) * mm});
            skArc(sketch, "E798", {"start": v(20.07, 6.17) * mm, "mid": v(19.97, 6.49) * mm, "end": v(19.87, 6.8) * mm});
            skArc(sketch, "E799", {"start": v(18.86, 9.24) * mm, "mid": v(18.71, 9.53) * mm, "end": v(18.56, 9.83) * mm});
            skArc(sketch, "E800", {"start": v(17.18, 12.07) * mm, "mid": v(16.99, 12.34) * mm, "end": v(16.8, 12.61) * mm});
            skArc(sketch, "E801", {"start": v(15.08, 14.61) * mm, "mid": v(14.85, 14.85) * mm, "end": v(14.61, 15.08) * mm});
            skArc(sketch, "E802", {"start": v(12.61, 16.8) * mm, "mid": v(12.34, 16.99) * mm, "end": v(12.07, 17.18) * mm});
            skArc(sketch, "E803", {"start": v(9.83, 18.56) * mm, "mid": v(9.53, 18.71) * mm, "end": v(9.24, 18.86) * mm});
            skArc(sketch, "E804", {"start": v(6.8, 19.87) * mm, "mid": v(6.49, 19.97) * mm, "end": v(6.17, 20.07) * mm});
            skArc(sketch, "E805", {"start": v(3.61, 20.69) * mm, "mid": v(3.29, 20.74) * mm, "end": v(2.96, 20.8) * mm});
            skArc(sketch, "E806", {"start": v(0.33, 21) * mm, "mid": v(0, 21) * mm, "end": v(-0.33, 21) * mm});
            skArc(sketch, "E807", {"start": v(-2.96, 20.8) * mm, "mid": v(-3.29, 20.74) * mm, "end": v(-3.61, 20.69) * mm});
            skArc(sketch, "E808", {"start": v(-6.17, 20.07) * mm, "mid": v(-6.49, 19.97) * mm, "end": v(-6.8, 19.87) * mm});
            skArc(sketch, "E809", {"start": v(-9.24, 18.86) * mm, "mid": v(-9.53, 18.71) * mm, "end": v(-9.83, 18.56) * mm});
            skArc(sketch, "E810", {"start": v(-12.07, 17.18) * mm, "mid": v(-12.34, 16.99) * mm, "end": v(-12.61, 16.8) * mm});
            skArc(sketch, "E811", {"start": v(-14.61, 15.08) * mm, "mid": v(-14.85, 14.85) * mm, "end": v(-15.08, 14.61) * mm});
            skArc(sketch, "E812", {"start": v(-16.8, 12.61) * mm, "mid": v(-16.99, 12.34) * mm, "end": v(-17.18, 12.07) * mm});
            skArc(sketch, "E813", {"start": v(-18.56, 9.83) * mm, "mid": v(-18.71, 9.53) * mm, "end": v(-18.86, 9.24) * mm});
            skArc(sketch, "E814", {"start": v(-19.87, 6.8) * mm, "mid": v(-19.97, 6.49) * mm, "end": v(-20.07, 6.17) * mm});
            skArc(sketch, "E815", {"start": v(-20.69, 3.61) * mm, "mid": v(-20.74, 3.29) * mm, "end": v(-20.8, 2.96) * mm});
            skArc(sketch, "E816", {"start": v(-21, 0.33) * mm, "mid": v(-21, 0.17) * mm, "end": v(-21, 0) * mm});
            skArc(sketch, "E817", {"start": v(-20.8, -2.96) * mm, "mid": v(-20.74, -3.29) * mm, "end": v(-20.69, -3.61) * mm});
            skArc(sketch, "E818", {"start": v(-20.07, -6.17) * mm, "mid": v(-19.97, -6.49) * mm, "end": v(-19.87, -6.8) * mm});
            skArc(sketch, "E819", {"start": v(-18.86, -9.24) * mm, "mid": v(-18.71, -9.53) * mm, "end": v(-18.56, -9.83) * mm});
            skArc(sketch, "E820", {"start": v(-17.18, -12.07) * mm, "mid": v(-16.99, -12.34) * mm, "end": v(-16.8, -12.61) * mm});
            skArc(sketch, "E821", {"start": v(-15.08, -14.61) * mm, "mid": v(-14.85, -14.85) * mm, "end": v(-14.61, -15.08) * mm});
            skArc(sketch, "E822", {"start": v(-12.61, -16.8) * mm, "mid": v(-12.34, -16.99) * mm, "end": v(-12.07, -17.18) * mm});
            skArc(sketch, "E823", {"start": v(-9.83, -18.56) * mm, "mid": v(-9.53, -18.71) * mm, "end": v(-9.24, -18.86) * mm});
            skArc(sketch, "E824", {"start": v(-6.8, -19.87) * mm, "mid": v(-6.49, -19.97) * mm, "end": v(-6.17, -20.07) * mm});
            skArc(sketch, "E825", {"start": v(-3.61, -20.69) * mm, "mid": v(-3.29, -20.74) * mm, "end": v(-2.96, -20.8) * mm});
            skArc(sketch, "E826", {"start": v(-0.33, -21) * mm, "mid": v(0, -21) * mm, "end": v(0.33, -21) * mm});
            skArc(sketch, "E827", {"start": v(2.96, -20.8) * mm, "mid": v(3.29, -20.74) * mm, "end": v(3.61, -20.69) * mm});
            skArc(sketch, "E828", {"start": v(6.17, -20.07) * mm, "mid": v(6.49, -19.97) * mm, "end": v(6.8, -19.87) * mm});
            skArc(sketch, "E829", {"start": v(9.24, -18.86) * mm, "mid": v(9.53, -18.71) * mm, "end": v(9.83, -18.56) * mm});
            skArc(sketch, "E830", {"start": v(12.07, -17.18) * mm, "mid": v(12.34, -16.99) * mm, "end": v(12.61, -16.8) * mm});
            skArc(sketch, "E831", {"start": v(14.61, -15.08) * mm, "mid": v(14.85, -14.85) * mm, "end": v(15.08, -14.61) * mm});
            skArc(sketch, "E832", {"start": v(16.8, -12.61) * mm, "mid": v(16.99, -12.34) * mm, "end": v(17.18, -12.07) * mm});
            skArc(sketch, "E833", {"start": v(18.56, -9.83) * mm, "mid": v(18.71, -9.53) * mm, "end": v(18.86, -9.24) * mm});
            skArc(sketch, "E834", {"start": v(19.87, -6.8) * mm, "mid": v(19.97, -6.49) * mm, "end": v(20.07, -6.17) * mm});
            skArc(sketch, "E835", {"start": v(20.69, -3.61) * mm, "mid": v(20.74, -3.29) * mm, "end": v(20.8, -2.96) * mm});
            skArc(sketch, "E836", {"start": v(0, 5) * mm, "mid": v(-5, 0) * mm, "end": v(0, -5) * mm});
            skLineSegment(sketch, "E837.0.0", {"start": v(7.8, 4.5) * mm, "end": v(0, 9) * mm});
            skLineSegment(sketch, "E837.0.1", {"start": v(0, 9) * mm, "end": v(-7.8, 4.5) * mm});
            skLineSegment(sketch, "E837.0.2", {"start": v(-7.8, 4.5) * mm, "end": v(-7.8, -4.5) * mm});
            skLineSegment(sketch, "E837.0.3", {"start": v(-7.8, -4.5) * mm, "end": v(0, -9) * mm});
            skLineSegment(sketch, "E837.0.4", {"start": v(0, -9) * mm, "end": v(7.8, -4.5) * mm});
            skLineSegment(sketch, "E837.0.5", {"start": v(7.8, -4.5) * mm, "end": v(7.8, 4.5) * mm});
            skSolve(sketch);
        }
        {
            var Q0;
            Q0=makeQuery(id+"F6.imprint","IMPRINT",FACE,{"disambiguationData":[TD([[makeQuery(id+"F6.imprint","IMPRINT",EDGE,{"derivedFrom":sQuery(id+"F6.wireOp",EDGE,"E513")}),1.0]])]});
            extrude(context, id + "F7", {"entities" : qUnion([Q0]), "depth" : 8 * mm});
        }
    });
